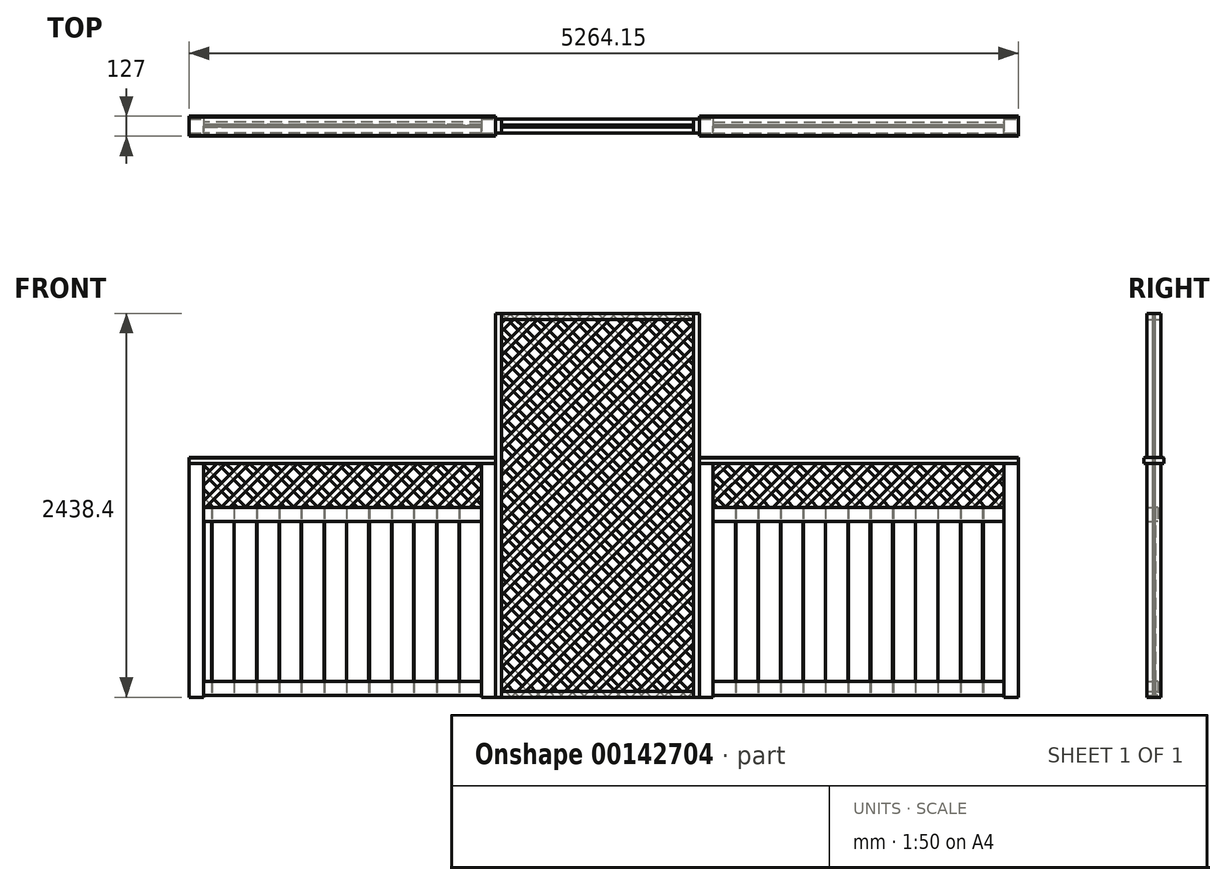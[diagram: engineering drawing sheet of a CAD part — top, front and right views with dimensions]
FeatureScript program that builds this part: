
annotation { "Feature Type Name" : "Feature", "Feature Type Description" : "" }
export const myFeature = defineFeature(function(context is Context, id is Id, definition is map)
    precondition{}
    {
        {
            var Q0;
            Q0=qCreatedBy(makeId("Top.planeOp"),FACE);
            var sketch = newSketch(context, id + "F0", { "sketchPlane" : qUnion([Q0])});
            skLineSegment(sketch, "E0", {"start": v(0, 0) * mm, "end": v(5334, 0) * mm, "construction": true});
            skLineSegment(sketch, "E1.bottom", {"start": v(38.1, 0) * mm, "end": v(127, 0) * mm});
            skLineSegment(sketch, "E1.top", {"start": v(38.1, -88.9) * mm, "end": v(127, -88.9) * mm});
            skLineSegment(sketch, "E1.left", {"start": v(38.1, 0) * mm, "end": v(38.1, -88.9) * mm});
            skLineSegment(sketch, "E1.right", {"start": v(127, 0) * mm, "end": v(127, -88.9) * mm});
            skLineSegment(sketch, "E2.bottom", {"start": v(1892.3, 0) * mm, "end": v(1981.2, 0) * mm});
            skLineSegment(sketch, "E2.top", {"start": v(1892.3, -88.9) * mm, "end": v(1981.2, -88.9) * mm});
            skLineSegment(sketch, "E2.left", {"start": v(1892.3, 0) * mm, "end": v(1892.3, -88.9) * mm});
            skLineSegment(sketch, "E2.right", {"start": v(1981.2, 0) * mm, "end": v(1981.2, -88.9) * mm});
            skLineSegment(sketch, "E3.bottom", {"start": v(3276.6, 0) * mm, "end": v(3365.5, 0) * mm});
            skLineSegment(sketch, "E3.top", {"start": v(3276.6, -88.9) * mm, "end": v(3365.5, -88.9) * mm});
            skLineSegment(sketch, "E3.left", {"start": v(3276.6, 0) * mm, "end": v(3276.6, -88.9) * mm});
            skLineSegment(sketch, "E3.right", {"start": v(3365.5, 0) * mm, "end": v(3365.5, -88.9) * mm});
            skLineSegment(sketch, "E4.bottom", {"start": v(5213.35, 0) * mm, "end": v(5302.25, 0) * mm});
            skLineSegment(sketch, "E4.top", {"start": v(5213.35, -88.9) * mm, "end": v(5302.25, -88.9) * mm});
            skLineSegment(sketch, "E4.left", {"start": v(5213.35, 0) * mm, "end": v(5213.35, -88.9) * mm});
            skLineSegment(sketch, "E4.right", {"start": v(5302.25, 0) * mm, "end": v(5302.25, -88.9) * mm});
            skSolve(sketch);
        }
        {
            var Q0;
            Q0 = qSketchRegion(id + "F0", true);
            extrude(context, id + "F1", {"entities" : qUnion([Q0]), "depth" : 1485.9 * mm});
        }
        {
            var Q0;
            Q0=makeQuery(id+"F1.opExtrude","SWEPT_FACE",FACE,{"disambiguationData":[OSD([sQuery(id+"F0.wireOp",EDGE,"E1.right")])]});
            var sketch = newSketch(context, id + "F2", { "sketchPlane" : qUnion([Q0])});
            skLineSegment(sketch, "E5.bottom", {"start": v(-88.9, 1206.5) * mm, "end": v(-50.8, 1206.5) * mm});
            skLineSegment(sketch, "E5.top", {"start": v(-88.9, 1117.6) * mm, "end": v(-50.8, 1117.6) * mm});
            skLineSegment(sketch, "E5.left", {"start": v(-88.9, 1206.5) * mm, "end": v(-88.9, 1117.6) * mm});
            skLineSegment(sketch, "E5.right", {"start": v(-50.8, 1206.5) * mm, "end": v(-50.8, 1117.6) * mm});
            skSolve(sketch);
        }
        {
            var Q0;
            Q0 = qSketchRegion(id + "F2", true);
            extrude(context, id + "F3", {"entities" : qUnion([Q0]), "depth" : 1765.3 * mm});
        }
        {
            var Q0;
            Q0=makeQuery(id+"F3.opExtrude","SWEPT_BODY",BODY,{"disambiguationData":[OSD([sQuery(id+"F2.wireOp",EDGE,"E5.bottom"),sQuery(id+"F2.wireOp",EDGE,"E5.top"),sQuery(id+"F2.wireOp",EDGE,"E5.left"),sQuery(id+"F2.wireOp",EDGE,"E5.right")])]});
            transform(context, id + "F4", {"entities" : qUnion([Q0]), "transformType" : TransformType.TRANSLATION_3D, "dx" : 0 * mm, "dy" : 0 * mm, "dz" : -1104.9 * mm, "makeCopy" : true});
        }
        {
            var Q0;
            Q0=makeQuery(id+"F1.opExtrude","SWEPT_FACE",FACE,{"disambiguationData":[OSD([sQuery(id+"F0.wireOp",EDGE,"E4.left")])]});
            var sketch = newSketch(context, id + "F5", { "sketchPlane" : qUnion([Q0])});
            skLineSegment(sketch, "E6.bottom", {"start": v(88.9, 1206.5) * mm, "end": v(50.8, 1206.5) * mm});
            skLineSegment(sketch, "E6.top", {"start": v(88.9, 1117.6) * mm, "end": v(50.8, 1117.6) * mm});
            skLineSegment(sketch, "E6.left", {"start": v(88.9, 1206.5) * mm, "end": v(88.9, 1117.6) * mm});
            skLineSegment(sketch, "E6.right", {"start": v(50.8, 1206.5) * mm, "end": v(50.8, 1117.6) * mm});
            skLineSegment(sketch, "E7.bottom", {"start": v(88.9, 101.6) * mm, "end": v(50.8, 101.6) * mm});
            skLineSegment(sketch, "E7.top", {"start": v(88.9, 12.7) * mm, "end": v(50.8, 12.7) * mm});
            skLineSegment(sketch, "E7.left", {"start": v(88.9, 101.6) * mm, "end": v(88.9, 12.7) * mm});
            skLineSegment(sketch, "E7.right", {"start": v(50.8, 101.6) * mm, "end": v(50.8, 12.7) * mm});
            skSolve(sketch);
        }
        {
            var Q0;
            Q0 = qSketchRegion(id + "F5", true);
            extrude(context, id + "F6", {"entities" : qUnion([Q0]), "depth" : 1847.85 * mm});
        }
        {
            var Q0;
            Q0=makeQuery(id+"F1.opExtrude","SWEPT_FACE",FACE,{"disambiguationData":[OSD([sQuery(id+"F0.wireOp",EDGE,"E2.top")])]});
            var sketch = newSketch(context, id + "F7", { "sketchPlane" : qUnion([Q0])});
            skLineSegment(sketch, "E8.bottom", {"start": v(1981.2, 0) * mm, "end": v(2019.3, 0) * mm});
            skLineSegment(sketch, "E8.top", {"start": v(1981.2, 2438.4) * mm, "end": v(2019.3, 2438.4) * mm});
            skLineSegment(sketch, "E8.left", {"start": v(1981.2, 0) * mm, "end": v(1981.2, 2438.4) * mm});
            skLineSegment(sketch, "E8.right", {"start": v(2019.3, 0) * mm, "end": v(2019.3, 2438.4) * mm});
            skSolve(sketch);
        }
        {
            var Q0;
            Q0 = qSketchRegion(id + "F7", true);
            extrude(context, id + "F8", {"entities" : qUnion([Q0]), "oppositeDirection" : true, "depth" : 88.9 * mm});
        }
        {
            var Q0;
            Q0=makeQuery(id+"F1.opExtrude","SWEPT_FACE",FACE,{"disambiguationData":[OSD([sQuery(id+"F0.wireOp",EDGE,"E3.top")])]});
            var sketch = newSketch(context, id + "F9", { "sketchPlane" : qUnion([Q0])});
            skLineSegment(sketch, "E9.bottom", {"start": v(3276.6, 0) * mm, "end": v(3238.5, 0) * mm});
            skLineSegment(sketch, "E9.top", {"start": v(3276.6, 2438.4) * mm, "end": v(3238.5, 2438.4) * mm});
            skLineSegment(sketch, "E9.left", {"start": v(3276.6, 0) * mm, "end": v(3276.6, 2438.4) * mm});
            skLineSegment(sketch, "E9.right", {"start": v(3238.5, 0) * mm, "end": v(3238.5, 2438.4) * mm});
            skSolve(sketch);
        }
        {
            var Q0;
            Q0 = qSketchRegion(id + "F9", true);
            extrude(context, id + "F10", {"entities" : qUnion([Q0]), "oppositeDirection" : true, "depth" : 88.9 * mm});
        }
        {
            var Q0;
            Q0=makeQuery(id+"F8.opExtrude","SWEPT_FACE",FACE,{"disambiguationData":[OSD([sQuery(id+"F7.wireOp",EDGE,"E8.right")])]});
            var sketch = newSketch(context, id + "F11", { "sketchPlane" : qUnion([Q0])});
            skLineSegment(sketch, "E10.bottom", {"start": v(-88.9, 2438.4) * mm, "end": v(-50.8, 2438.4) * mm});
            skLineSegment(sketch, "E10.top", {"start": v(-88.9, 2400.3) * mm, "end": v(-50.8, 2400.3) * mm});
            skLineSegment(sketch, "E10.left", {"start": v(-88.9, 2438.4) * mm, "end": v(-88.9, 2400.3) * mm});
            skLineSegment(sketch, "E10.right", {"start": v(0, 2438.4) * mm, "end": v(0, 2400.3) * mm});
            skLineSegment(sketch, "E11.bottom", {"start": v(-88.9, 0) * mm, "end": v(-50.8, 0) * mm});
            skLineSegment(sketch, "E11.top", {"start": v(-88.9, 38.1) * mm, "end": v(-50.8, 38.1) * mm});
            skLineSegment(sketch, "E11.left", {"start": v(-88.9, 0) * mm, "end": v(-88.9, 38.1) * mm});
            skLineSegment(sketch, "E11.right", {"start": v(0, 0) * mm, "end": v(0, 38.1) * mm});
            skLineSegment(sketch, "E12", {"start": v(-50.8, 2438.4) * mm, "end": v(-50.8, 2400.3) * mm});
            skLineSegment(sketch, "E13", {"start": v(-38.1, 2438.4) * mm, "end": v(-38.1, 2400.3) * mm});
            skLineSegment(sketch, "E14.trimOffspring", {"start": v(-38.1, 2438.4) * mm, "end": v(0, 2438.4) * mm});
            skLineSegment(sketch, "E15.trimOffspring", {"start": v(-38.1, 2400.3) * mm, "end": v(0, 2400.3) * mm});
            skLineSegment(sketch, "E16", {"start": v(-50.8, 38.1) * mm, "end": v(-50.8, 0) * mm});
            skLineSegment(sketch, "E17", {"start": v(-38.1, 38.1) * mm, "end": v(-38.1, 0) * mm});
            skLineSegment(sketch, "E18.trimOffspring", {"start": v(-38.1, 38.1) * mm, "end": v(0, 38.1) * mm});
            skLineSegment(sketch, "E19.trimOffspring", {"start": v(-38.1, 0) * mm, "end": v(0, 0) * mm});
            skSolve(sketch);
        }
        {
            var Q0;
            Q0 = qSketchRegion(id + "F11", true);
            extrude(context, id + "F12", {"entities" : qUnion([Q0]), "depth" : 1219.2 * mm});
        }
        {
            var Q0;
            Q0=makeQuery(id+"F8.opExtrude","CAP_FACE",FACE,{"disambiguationData":[OSD([sQuery(id+"F7.wireOp",EDGE,"E8.bottom"),sQuery(id+"F7.wireOp",EDGE,"E8.top"),sQuery(id+"F7.wireOp",EDGE,"E8.left"),sQuery(id+"F7.wireOp",EDGE,"E8.right")])],"isStart":true});
            cPlane(context, id + "F13", {"entities" : qUnion([Q0]), "cplaneType" : CPlaneType.OFFSET, "offset" : 44.45 * mm, "oppositeDirection" : true, "width" : 152.4 * mm, "height" : 152.4 * mm});
        }
        {
            var Q0;
            Q0=qCreatedBy(id+"F13.planeOp",FACE);
            var sketch = newSketch(context, id + "F14", { "sketchPlane" : qUnion([Q0])});
            skLineSegment(sketch, "E20.bottom", {"start": v(2019.3, 0) * mm, "end": v(3238.5, 0) * mm, "construction": true});
            skLineSegment(sketch, "E20.top", {"start": v(2019.3, 2438.4) * mm, "end": v(3238.5, 2438.4) * mm, "construction": true});
            skLineSegment(sketch, "E20.left", {"start": v(2019.3, 0) * mm, "end": v(2019.3, 2438.4) * mm, "construction": true});
            skLineSegment(sketch, "E20.right", {"start": v(3238.5, 0) * mm, "end": v(3238.5, 2438.4) * mm, "construction": true});
            skLineSegment(sketch, "E21", {"start": v(3201.94, 0) * mm, "end": v(3238.5, 36.56) * mm});
            skLineSegment(sketch, "E22", {"start": v(3238.5, 90.44) * mm, "end": v(3148.06, 0) * mm});
            skLineSegment(sketch, "E23.0.1.0", {"start": v(4481.56, 1485.9) * mm, "end": v(4202.16, 1206.5) * mm});
            skLineSegment(sketch, "E23.0.1.1", {"start": v(3049.54, 0) * mm, "end": v(3238.5, 188.96) * mm});
            skLineSegment(sketch, "E23.0.2.0", {"start": v(4329.16, 1485.9) * mm, "end": v(4049.76, 1206.5) * mm});
            skLineSegment(sketch, "E23.0.2.1", {"start": v(2897.14, 0) * mm, "end": v(3238.5, 341.36) * mm});
            skLineSegment(sketch, "E23.0.3.0", {"start": v(4176.76, 1485.9) * mm, "end": v(3897.36, 1206.5) * mm});
            skLineSegment(sketch, "E23.0.3.1", {"start": v(2744.74, 0) * mm, "end": v(3238.5, 493.76) * mm});
            skLineSegment(sketch, "E23.0.4.0", {"start": v(4024.36, 1485.9) * mm, "end": v(3744.96, 1206.5) * mm});
            skLineSegment(sketch, "E23.0.4.1", {"start": v(2592.34, 0) * mm, "end": v(3238.5, 646.16) * mm});
            skLineSegment(sketch, "E23.0.5.0", {"start": v(3871.96, 1485.9) * mm, "end": v(3592.56, 1206.5) * mm});
            skLineSegment(sketch, "E23.0.5.1", {"start": v(2439.94, 0) * mm, "end": v(3238.5, 798.56) * mm});
            skLineSegment(sketch, "E23.0.6.0", {"start": v(3719.56, 1485.9) * mm, "end": v(3440.16, 1206.5) * mm});
            skLineSegment(sketch, "E23.0.6.1", {"start": v(2287.54, 0) * mm, "end": v(3238.5, 950.96) * mm});
            skLineSegment(sketch, "E23.0.7.0", {"start": v(3567.16, 1485.9) * mm, "end": v(3365.5, 1284.24) * mm});
            skLineSegment(sketch, "E23.0.7.1", {"start": v(2135.14, 0) * mm, "end": v(3238.5, 1103.36) * mm});
            skLineSegment(sketch, "E23.0.8.0", {"start": v(3414.76, 1485.9) * mm, "end": v(3365.5, 1436.64) * mm});
            skLineSegment(sketch, "E23.0.8.1", {"start": v(2019.3, 36.56) * mm, "end": v(3238.5, 1255.76) * mm});
            skLineSegment(sketch, "E23.0.9.0", {"start": v(3238.5, 1462.04) * mm, "end": v(2019.3, 242.84) * mm});
            skLineSegment(sketch, "E23.0.9.1", {"start": v(2019.3, 188.96) * mm, "end": v(3238.5, 1408.16) * mm});
            skLineSegment(sketch, "E23.0.10.0", {"start": v(3238.5, 1614.44) * mm, "end": v(2019.3, 395.24) * mm});
            skLineSegment(sketch, "E23.0.10.1", {"start": v(2019.3, 341.36) * mm, "end": v(3238.5, 1560.56) * mm});
            skLineSegment(sketch, "E23.0.11.0", {"start": v(3238.5, 1766.84) * mm, "end": v(2019.3, 547.64) * mm});
            skLineSegment(sketch, "E23.0.11.1", {"start": v(2019.3, 493.76) * mm, "end": v(3238.5, 1712.96) * mm});
            skLineSegment(sketch, "E23.0.12.0", {"start": v(3238.5, 1919.24) * mm, "end": v(2019.3, 700.04) * mm});
            skLineSegment(sketch, "E23.0.12.1", {"start": v(2019.3, 646.16) * mm, "end": v(3238.5, 1865.36) * mm});
            skLineSegment(sketch, "E23.0.13.0", {"start": v(3238.5, 2071.64) * mm, "end": v(2019.3, 852.44) * mm});
            skLineSegment(sketch, "E23.0.13.1", {"start": v(2019.3, 798.56) * mm, "end": v(3238.5, 2017.76) * mm});
            skLineSegment(sketch, "E23.0.14.0", {"start": v(3238.5, 2224.04) * mm, "end": v(2019.3, 1004.84) * mm});
            skLineSegment(sketch, "E23.0.14.1", {"start": v(2019.3, 950.96) * mm, "end": v(3238.5, 2170.16) * mm});
            skLineSegment(sketch, "E23.0.15.0", {"start": v(3238.5, 2376.44) * mm, "end": v(2019.3, 1157.24) * mm});
            skLineSegment(sketch, "E23.0.15.1", {"start": v(2019.3, 1103.36) * mm, "end": v(3238.5, 2322.56) * mm});
            skLineSegment(sketch, "E23.0.16.0", {"start": v(3148.06, 2438.4) * mm, "end": v(2019.3, 1309.64) * mm});
            skLineSegment(sketch, "E23.0.16.1", {"start": v(2019.3, 1255.76) * mm, "end": v(3201.94, 2438.4) * mm});
            skLineSegment(sketch, "E23.0.17.0", {"start": v(2995.66, 2438.4) * mm, "end": v(2019.3, 1462.04) * mm});
            skLineSegment(sketch, "E23.0.17.1", {"start": v(1817.64, 1206.5) * mm, "end": v(1892.3, 1281.16) * mm});
            skLineSegment(sketch, "E23.0.18.0", {"start": v(2843.26, 2438.4) * mm, "end": v(2019.3, 1614.44) * mm});
            skLineSegment(sketch, "E23.0.18.1", {"start": v(1665.24, 1206.5) * mm, "end": v(1892.3, 1433.56) * mm});
            skLineSegment(sketch, "E23.0.19.0", {"start": v(2690.86, 2438.4) * mm, "end": v(2019.3, 1766.84) * mm});
            skLineSegment(sketch, "E23.0.19.1", {"start": v(1512.84, 1206.5) * mm, "end": v(1792.24, 1485.9) * mm});
            skLineSegment(sketch, "E23.0.20.0", {"start": v(2538.46, 2438.4) * mm, "end": v(2019.3, 1919.24) * mm});
            skLineSegment(sketch, "E23.0.20.1", {"start": v(2019.3, 1865.36) * mm, "end": v(2592.34, 2438.4) * mm});
            skLineSegment(sketch, "E23.0.21.0", {"start": v(2386.06, 2438.4) * mm, "end": v(2019.3, 2071.64) * mm});
            skLineSegment(sketch, "E23.0.21.1", {"start": v(2019.3, 2017.76) * mm, "end": v(2439.94, 2438.4) * mm});
            skLineSegment(sketch, "E23.0.22.0", {"start": v(2233.66, 2438.4) * mm, "end": v(2019.3, 2224.04) * mm});
            skLineSegment(sketch, "E23.0.22.1", {"start": v(2019.3, 2170.16) * mm, "end": v(2287.54, 2438.4) * mm});
            skLineSegment(sketch, "E23.0.23.0", {"start": v(2081.26, 2438.4) * mm, "end": v(2019.3, 2376.44) * mm});
            skLineSegment(sketch, "E23.0.23.1", {"start": v(2019.3, 2322.56) * mm, "end": v(2135.14, 2438.4) * mm});
            skLineSegment(sketch, "E23.direction2", {"start": v(3238.5, 90.44) * mm, "end": v(3238.5, 242.84) * mm, "construction": true});
            skPoint(sketch, "E24.start.orphan", {"position": v(3265.44, 63.5) * mm});
            skLineSegment(sketch, "E25", {"start": v(2081.26, 2438.4) * mm, "end": v(2135.14, 2438.4) * mm});
            skLineSegment(sketch, "E26", {"start": v(2233.66, 2438.4) * mm, "end": v(2287.54, 2438.4) * mm});
            skLineSegment(sketch, "E27", {"start": v(2386.06, 2438.4) * mm, "end": v(2439.94, 2438.4) * mm});
            skLineSegment(sketch, "E28", {"start": v(2538.46, 2438.4) * mm, "end": v(2592.34, 2438.4) * mm});
            skLineSegment(sketch, "E29", {"start": v(2690.86, 2438.4) * mm, "end": v(2744.74, 2438.4) * mm});
            skLineSegment(sketch, "E30", {"start": v(2843.26, 2438.4) * mm, "end": v(2897.14, 2438.4) * mm});
            skLineSegment(sketch, "E31", {"start": v(2995.66, 2438.4) * mm, "end": v(3049.54, 2438.4) * mm});
            skLineSegment(sketch, "E32", {"start": v(3148.06, 2438.4) * mm, "end": v(3201.94, 2438.4) * mm});
            skLineSegment(sketch, "E33", {"start": v(3238.5, 2376.44) * mm, "end": v(3238.5, 2322.56) * mm});
            skLineSegment(sketch, "E34", {"start": v(3238.5, 2224.04) * mm, "end": v(3238.5, 2170.16) * mm});
            skLineSegment(sketch, "E35", {"start": v(3238.5, 2071.64) * mm, "end": v(3238.5, 2017.76) * mm});
            skLineSegment(sketch, "E36", {"start": v(3238.5, 1919.24) * mm, "end": v(3238.5, 1865.36) * mm});
            skLineSegment(sketch, "E37", {"start": v(3238.5, 1766.84) * mm, "end": v(3238.5, 1712.96) * mm});
            skLineSegment(sketch, "E38", {"start": v(3238.5, 1614.44) * mm, "end": v(3238.5, 1560.56) * mm});
            skLineSegment(sketch, "E39", {"start": v(3238.5, 1462.04) * mm, "end": v(3238.5, 1408.16) * mm});
            skLineSegment(sketch, "E40", {"start": v(3238.5, 1309.64) * mm, "end": v(3238.5, 1255.76) * mm});
            skLineSegment(sketch, "E41", {"start": v(3238.5, 1157.24) * mm, "end": v(3238.5, 1103.36) * mm});
            skLineSegment(sketch, "E42", {"start": v(3238.5, 1004.84) * mm, "end": v(3238.5, 950.96) * mm});
            skLineSegment(sketch, "E43", {"start": v(3238.5, 852.44) * mm, "end": v(3238.5, 798.56) * mm});
            skLineSegment(sketch, "E44", {"start": v(3238.5, 700.04) * mm, "end": v(3238.5, 646.16) * mm});
            skLineSegment(sketch, "E45", {"start": v(3238.5, 547.64) * mm, "end": v(3238.5, 493.76) * mm});
            skLineSegment(sketch, "E46", {"start": v(3238.5, 395.24) * mm, "end": v(3238.5, 341.36) * mm});
            skLineSegment(sketch, "E47", {"start": v(3238.5, 242.84) * mm, "end": v(3238.5, 188.96) * mm});
            skLineSegment(sketch, "E48", {"start": v(3238.5, 36.56) * mm, "end": v(3238.5, 90.44) * mm});
            skLineSegment(sketch, "E49", {"start": v(3201.94, 0) * mm, "end": v(3148.06, 0) * mm});
            skLineSegment(sketch, "E50", {"start": v(3049.54, 0) * mm, "end": v(2995.66, 0) * mm});
            skLineSegment(sketch, "E51", {"start": v(2897.14, 0) * mm, "end": v(2843.26, 0) * mm});
            skLineSegment(sketch, "E52", {"start": v(2744.74, 0) * mm, "end": v(2690.86, 0) * mm});
            skLineSegment(sketch, "E53", {"start": v(2592.34, 0) * mm, "end": v(2538.46, 0) * mm});
            skLineSegment(sketch, "E54", {"start": v(2439.94, 0) * mm, "end": v(2386.06, 0) * mm});
            skLineSegment(sketch, "E55", {"start": v(2287.54, 0) * mm, "end": v(2233.66, 0) * mm});
            skLineSegment(sketch, "E56", {"start": v(2135.14, 0) * mm, "end": v(2081.26, 0) * mm});
            skLineSegment(sketch, "E57", {"start": v(2019.3, 36.56) * mm, "end": v(2019.3, 90.44) * mm});
            skLineSegment(sketch, "E58", {"start": v(2019.3, 188.96) * mm, "end": v(2019.3, 242.84) * mm});
            skLineSegment(sketch, "E59", {"start": v(2019.3, 341.36) * mm, "end": v(2019.3, 395.24) * mm});
            skLineSegment(sketch, "E60", {"start": v(2019.3, 493.76) * mm, "end": v(2019.3, 547.64) * mm});
            skLineSegment(sketch, "E61", {"start": v(2019.3, 646.16) * mm, "end": v(2019.3, 700.04) * mm});
            skLineSegment(sketch, "E62", {"start": v(2019.3, 798.56) * mm, "end": v(2019.3, 852.44) * mm});
            skLineSegment(sketch, "E63", {"start": v(2019.3, 950.96) * mm, "end": v(2019.3, 1004.84) * mm});
            skLineSegment(sketch, "E64", {"start": v(2019.3, 1103.36) * mm, "end": v(2019.3, 1157.24) * mm});
            skLineSegment(sketch, "E65", {"start": v(2019.3, 1255.76) * mm, "end": v(2019.3, 1309.64) * mm});
            skLineSegment(sketch, "E66", {"start": v(2019.3, 1408.16) * mm, "end": v(2019.3, 1462.04) * mm});
            skLineSegment(sketch, "E67", {"start": v(2019.3, 1560.56) * mm, "end": v(2019.3, 1614.44) * mm});
            skLineSegment(sketch, "E68", {"start": v(2019.3, 1712.96) * mm, "end": v(2019.3, 1766.84) * mm});
            skLineSegment(sketch, "E69", {"start": v(2019.3, 1865.36) * mm, "end": v(2019.3, 1919.24) * mm});
            skLineSegment(sketch, "E70", {"start": v(2019.3, 2017.76) * mm, "end": v(2019.3, 2071.64) * mm});
            skLineSegment(sketch, "E71", {"start": v(2019.3, 2170.16) * mm, "end": v(2019.3, 2224.04) * mm});
            skLineSegment(sketch, "E72", {"start": v(2019.3, 2322.56) * mm, "end": v(2019.3, 2376.44) * mm});
            skLineSegment(sketch, "E73.bottom", {"start": v(1892.3, 1485.9) * mm, "end": v(127, 1485.9) * mm, "construction": true});
            skLineSegment(sketch, "E73.top", {"start": v(1892.3, 1206.5) * mm, "end": v(127, 1206.5) * mm, "construction": true});
            skLineSegment(sketch, "E73.left", {"start": v(1892.3, 1485.9) * mm, "end": v(1892.3, 1206.5) * mm, "construction": true});
            skLineSegment(sketch, "E73.right", {"start": v(127, 1485.9) * mm, "end": v(127, 1206.5) * mm, "construction": true});
            skLineSegment(sketch, "E74.trimOffspring", {"start": v(1890.76, 1485.9) * mm, "end": v(1611.36, 1206.5) * mm});
            skLineSegment(sketch, "E75.trimOffspring", {"start": v(2019.3, 1560.56) * mm, "end": v(2897.14, 2438.4) * mm});
            skLineSegment(sketch, "E76.trimOffspring", {"start": v(1892.3, 1335.04) * mm, "end": v(1763.76, 1206.5) * mm});
            skLineSegment(sketch, "E77.trimOffspring", {"start": v(2019.3, 1408.16) * mm, "end": v(3049.54, 2438.4) * mm});
            skLineSegment(sketch, "E78", {"start": v(1892.3, 1433.56) * mm, "end": v(1892.3, 1485.9) * mm});
            skLineSegment(sketch, "E79", {"start": v(1892.3, 1281.16) * mm, "end": v(1892.3, 1335.04) * mm});
            skLineSegment(sketch, "E80", {"start": v(1817.64, 1206.5) * mm, "end": v(1763.76, 1206.5) * mm});
            skLineSegment(sketch, "E81", {"start": v(1665.24, 1206.5) * mm, "end": v(1611.36, 1206.5) * mm});
            skLineSegment(sketch, "E82", {"start": v(1611.36, 1206.5) * mm, "end": v(1665.24, 1206.5) * mm});
            skLineSegment(sketch, "E83", {"start": v(1890.76, 1485.9) * mm, "end": v(1892.3, 1485.9) * mm});
            skLineSegment(sketch, "E84.trimOffspring", {"start": v(1738.36, 1485.9) * mm, "end": v(1458.96, 1206.5) * mm});
            skLineSegment(sketch, "E85.trimOffspring", {"start": v(2019.3, 1712.96) * mm, "end": v(2744.74, 2438.4) * mm});
            skLineSegment(sketch, "E86", {"start": v(1792.24, 1485.9) * mm, "end": v(1738.36, 1485.9) * mm});
            skLineSegment(sketch, "E87", {"start": v(1512.84, 1206.5) * mm, "end": v(1458.96, 1206.5) * mm});
            skLineSegment(sketch, "E88.1.0.0", {"start": v(1360.44, 1206.5) * mm, "end": v(1639.84, 1485.9) * mm});
            skLineSegment(sketch, "E88.1.0.1", {"start": v(1585.96, 1485.9) * mm, "end": v(1306.56, 1206.5) * mm});
            skLineSegment(sketch, "E88.2.0.0", {"start": v(1208.04, 1206.5) * mm, "end": v(1487.44, 1485.9) * mm});
            skLineSegment(sketch, "E88.2.0.1", {"start": v(1433.56, 1485.9) * mm, "end": v(1154.16, 1206.5) * mm});
            skLineSegment(sketch, "E88.3.0.0", {"start": v(1055.64, 1206.5) * mm, "end": v(1335.04, 1485.9) * mm});
            skLineSegment(sketch, "E88.3.0.1", {"start": v(1281.16, 1485.9) * mm, "end": v(1001.76, 1206.5) * mm});
            skLineSegment(sketch, "E88.4.0.0", {"start": v(903.24, 1206.5) * mm, "end": v(1182.64, 1485.9) * mm});
            skLineSegment(sketch, "E88.4.0.1", {"start": v(1128.76, 1485.9) * mm, "end": v(849.36, 1206.5) * mm});
            skLineSegment(sketch, "E88.5.0.0", {"start": v(750.84, 1206.5) * mm, "end": v(1030.24, 1485.9) * mm});
            skLineSegment(sketch, "E88.5.0.1", {"start": v(976.36, 1485.9) * mm, "end": v(696.96, 1206.5) * mm});
            skLineSegment(sketch, "E88.6.0.0", {"start": v(598.44, 1206.5) * mm, "end": v(877.84, 1485.9) * mm});
            skLineSegment(sketch, "E88.6.0.1", {"start": v(823.96, 1485.9) * mm, "end": v(544.56, 1206.5) * mm});
            skLineSegment(sketch, "E88.7.0.0", {"start": v(446.04, 1206.5) * mm, "end": v(725.44, 1485.9) * mm});
            skLineSegment(sketch, "E88.7.0.1", {"start": v(671.56, 1485.9) * mm, "end": v(392.16, 1206.5) * mm});
            skLineSegment(sketch, "E88.8.0.0", {"start": v(293.64, 1206.5) * mm, "end": v(573.04, 1485.9) * mm});
            skLineSegment(sketch, "E88.8.0.1", {"start": v(519.16, 1485.9) * mm, "end": v(239.76, 1206.5) * mm});
            skLineSegment(sketch, "E88.9.0.0", {"start": v(141.24, 1206.5) * mm, "end": v(420.64, 1485.9) * mm});
            skLineSegment(sketch, "E88.9.0.1", {"start": v(366.76, 1485.9) * mm, "end": v(127, 1246.14) * mm});
            skLineSegment(sketch, "E88.10.0.0", {"start": v(127, 1344.66) * mm, "end": v(268.24, 1485.9) * mm});
            skLineSegment(sketch, "E88.10.0.1", {"start": v(214.36, 1485.9) * mm, "end": v(127, 1398.54) * mm});
            skLineSegment(sketch, "E88.direction1", {"start": v(1512.84, 1206.5) * mm, "end": v(1360.44, 1206.5) * mm, "construction": true});
            skLineSegment(sketch, "E89", {"start": v(1360.44, 1206.5) * mm, "end": v(1306.56, 1206.5) * mm});
            skLineSegment(sketch, "E90", {"start": v(1208.04, 1206.5) * mm, "end": v(1154.16, 1206.5) * mm});
            skLineSegment(sketch, "E91", {"start": v(1639.84, 1485.9) * mm, "end": v(1585.96, 1485.9) * mm});
            skLineSegment(sketch, "E92", {"start": v(1487.44, 1485.9) * mm, "end": v(1433.56, 1485.9) * mm});
            skLineSegment(sketch, "E93", {"start": v(1335.04, 1485.9) * mm, "end": v(1281.16, 1485.9) * mm});
            skLineSegment(sketch, "E94", {"start": v(1182.64, 1485.9) * mm, "end": v(1128.76, 1485.9) * mm});
            skLineSegment(sketch, "E95", {"start": v(1030.24, 1485.9) * mm, "end": v(976.36, 1485.9) * mm});
            skLineSegment(sketch, "E96", {"start": v(1055.64, 1206.5) * mm, "end": v(1001.76, 1206.5) * mm});
            skLineSegment(sketch, "E97", {"start": v(544.56, 1206.5) * mm, "end": v(598.44, 1206.5) * mm});
            skLineSegment(sketch, "E98", {"start": v(696.96, 1206.5) * mm, "end": v(750.84, 1206.5) * mm});
            skLineSegment(sketch, "E99", {"start": v(849.36, 1206.5) * mm, "end": v(903.24, 1206.5) * mm});
            skLineSegment(sketch, "E100", {"start": v(366.76, 1485.9) * mm, "end": v(420.64, 1485.9) * mm});
            skLineSegment(sketch, "E101", {"start": v(519.16, 1485.9) * mm, "end": v(573.04, 1485.9) * mm});
            skLineSegment(sketch, "E102", {"start": v(671.56, 1485.9) * mm, "end": v(725.44, 1485.9) * mm});
            skLineSegment(sketch, "E103", {"start": v(823.96, 1485.9) * mm, "end": v(877.84, 1485.9) * mm});
            skLineSegment(sketch, "E104", {"start": v(446.04, 1206.5) * mm, "end": v(392.16, 1206.5) * mm});
            skLineSegment(sketch, "E105", {"start": v(293.64, 1206.5) * mm, "end": v(239.76, 1206.5) * mm});
            skLineSegment(sketch, "E106", {"start": v(141.24, 1206.5) * mm, "end": v(127, 1206.5) * mm});
            skLineSegment(sketch, "E107", {"start": v(127, 1398.54) * mm, "end": v(127, 1344.66) * mm});
            skLineSegment(sketch, "E108", {"start": v(268.24, 1485.9) * mm, "end": v(214.36, 1485.9) * mm});
            skLineSegment(sketch, "E109", {"start": v(127, 1246.14) * mm, "end": v(127, 1206.5) * mm});
            skLineSegment(sketch, "E110.bottom", {"start": v(3365.5, 1485.9) * mm, "end": v(5213.35, 1485.9) * mm, "construction": true});
            skLineSegment(sketch, "E110.top", {"start": v(3365.5, 1206.5) * mm, "end": v(5213.35, 1206.5) * mm, "construction": true});
            skLineSegment(sketch, "E110.left", {"start": v(3365.5, 1485.9) * mm, "end": v(3365.5, 1206.5) * mm, "construction": true});
            skLineSegment(sketch, "E110.right", {"start": v(5213.35, 1485.9) * mm, "end": v(5213.35, 1206.5) * mm, "construction": true});
            skLineSegment(sketch, "E111.trimOffspring", {"start": v(4256.04, 1206.5) * mm, "end": v(4535.44, 1485.9) * mm});
            skLineSegment(sketch, "E112.trimOffspring", {"start": v(3238.5, 242.84) * mm, "end": v(2995.66, 0) * mm});
            skLineSegment(sketch, "E113.trimOffspring", {"start": v(4103.64, 1206.5) * mm, "end": v(4383.04, 1485.9) * mm});
            skLineSegment(sketch, "E114.trimOffspring", {"start": v(3238.5, 395.24) * mm, "end": v(2843.26, 0) * mm});
            skLineSegment(sketch, "E115.trimOffspring", {"start": v(3951.24, 1206.5) * mm, "end": v(4230.64, 1485.9) * mm});
            skLineSegment(sketch, "E116.trimOffspring", {"start": v(3238.5, 547.64) * mm, "end": v(2690.86, 0) * mm});
            skLineSegment(sketch, "E117.trimOffspring", {"start": v(3238.5, 700.04) * mm, "end": v(2538.46, 0) * mm});
            skLineSegment(sketch, "E118.trimOffspring", {"start": v(3494.04, 1206.5) * mm, "end": v(3773.44, 1485.9) * mm});
            skLineSegment(sketch, "E119.trimOffspring", {"start": v(3238.5, 1004.84) * mm, "end": v(2233.66, 0) * mm});
            skLineSegment(sketch, "E120.trimOffspring", {"start": v(3798.84, 1206.5) * mm, "end": v(4078.24, 1485.9) * mm});
            skLineSegment(sketch, "E121.trimOffspring", {"start": v(3646.44, 1206.5) * mm, "end": v(3925.84, 1485.9) * mm});
            skLineSegment(sketch, "E122.trimOffspring", {"start": v(3238.5, 852.44) * mm, "end": v(2386.06, 0) * mm});
            skLineSegment(sketch, "E123.trimOffspring", {"start": v(3238.5, 1309.64) * mm, "end": v(2019.3, 90.44) * mm});
            skLineSegment(sketch, "E124.trimOffspring", {"start": v(3365.5, 1382.76) * mm, "end": v(3468.64, 1485.9) * mm});
            skLineSegment(sketch, "E125.trimOffspring", {"start": v(3238.5, 1157.24) * mm, "end": v(2081.26, 0) * mm});
            skLineSegment(sketch, "E126.trimOffspring", {"start": v(3365.5, 1230.36) * mm, "end": v(3621.04, 1485.9) * mm});
            skLineSegment(sketch, "E127.1.0.0", {"start": v(4633.96, 1485.9) * mm, "end": v(4354.56, 1206.5) * mm});
            skLineSegment(sketch, "E127.1.0.1", {"start": v(4408.44, 1206.5) * mm, "end": v(4687.84, 1485.9) * mm});
            skLineSegment(sketch, "E127.2.0.0", {"start": v(4786.36, 1485.9) * mm, "end": v(4506.96, 1206.5) * mm});
            skLineSegment(sketch, "E127.2.0.1", {"start": v(4560.84, 1206.5) * mm, "end": v(4840.24, 1485.9) * mm});
            skLineSegment(sketch, "E127.3.0.0", {"start": v(4938.76, 1485.9) * mm, "end": v(4659.36, 1206.5) * mm});
            skLineSegment(sketch, "E127.3.0.1", {"start": v(4713.24, 1206.5) * mm, "end": v(4992.64, 1485.9) * mm});
            skLineSegment(sketch, "E127.4.0.0", {"start": v(5091.16, 1485.9) * mm, "end": v(4811.76, 1206.5) * mm});
            skLineSegment(sketch, "E127.4.0.1", {"start": v(4865.64, 1206.5) * mm, "end": v(5145.04, 1485.9) * mm});
            skLineSegment(sketch, "E127.5.0.0", {"start": v(5213.35, 1455.7) * mm, "end": v(4964.16, 1206.5) * mm});
            skLineSegment(sketch, "E127.5.0.1", {"start": v(5018.04, 1206.5) * mm, "end": v(5213.35, 1401.8) * mm});
            skLineSegment(sketch, "E127.6.0.0", {"start": v(5213.35, 1303.3) * mm, "end": v(5116.56, 1206.5) * mm});
            skLineSegment(sketch, "E127.6.0.1", {"start": v(5170.44, 1206.5) * mm, "end": v(5213.35, 1249.4) * mm});
            skLineSegment(sketch, "E127.direction1", {"start": v(4202.16, 1206.5) * mm, "end": v(4354.56, 1206.5) * mm, "construction": true});
            skLineSegment(sketch, "E128", {"start": v(5213.35, 1455.7) * mm, "end": v(5213.35, 1401.8) * mm});
            skLineSegment(sketch, "E129", {"start": v(5213.35, 1303.3) * mm, "end": v(5213.35, 1249.4) * mm});
            skLineSegment(sketch, "E130", {"start": v(5170.44, 1206.5) * mm, "end": v(5116.56, 1206.5) * mm});
            skLineSegment(sketch, "E131", {"start": v(5018.04, 1206.5) * mm, "end": v(4964.16, 1206.5) * mm});
            skLineSegment(sketch, "E132", {"start": v(4865.64, 1206.5) * mm, "end": v(4811.76, 1206.5) * mm});
            skLineSegment(sketch, "E133", {"start": v(4713.24, 1206.5) * mm, "end": v(4659.36, 1206.5) * mm});
            skLineSegment(sketch, "E134", {"start": v(4560.84, 1206.5) * mm, "end": v(4506.96, 1206.5) * mm});
            skLineSegment(sketch, "E135", {"start": v(4633.96, 1485.9) * mm, "end": v(4687.84, 1485.9) * mm});
            skLineSegment(sketch, "E136", {"start": v(4786.36, 1485.9) * mm, "end": v(4840.24, 1485.9) * mm});
            skLineSegment(sketch, "E137", {"start": v(4938.76, 1485.9) * mm, "end": v(4992.64, 1485.9) * mm});
            skLineSegment(sketch, "E138", {"start": v(5091.16, 1485.9) * mm, "end": v(5145.04, 1485.9) * mm});
            skLineSegment(sketch, "E139", {"start": v(3365.5, 1436.64) * mm, "end": v(3365.5, 1382.76) * mm});
            skLineSegment(sketch, "E140", {"start": v(3365.5, 1230.36) * mm, "end": v(3365.5, 1284.24) * mm});
            skLineSegment(sketch, "E141", {"start": v(3440.16, 1206.5) * mm, "end": v(3494.04, 1206.5) * mm});
            skLineSegment(sketch, "E142", {"start": v(3592.56, 1206.5) * mm, "end": v(3646.44, 1206.5) * mm});
            skLineSegment(sketch, "E143", {"start": v(3744.96, 1206.5) * mm, "end": v(3798.84, 1206.5) * mm});
            skLineSegment(sketch, "E144", {"start": v(3897.36, 1206.5) * mm, "end": v(3951.24, 1206.5) * mm});
            skLineSegment(sketch, "E145", {"start": v(4049.76, 1206.5) * mm, "end": v(4103.64, 1206.5) * mm});
            skLineSegment(sketch, "E146", {"start": v(4202.16, 1206.5) * mm, "end": v(4256.04, 1206.5) * mm});
            skLineSegment(sketch, "E147", {"start": v(3414.76, 1485.9) * mm, "end": v(3468.64, 1485.9) * mm});
            skLineSegment(sketch, "E148", {"start": v(3567.16, 1485.9) * mm, "end": v(3621.04, 1485.9) * mm});
            skLineSegment(sketch, "E149", {"start": v(3719.56, 1485.9) * mm, "end": v(3773.44, 1485.9) * mm});
            skLineSegment(sketch, "E150", {"start": v(3871.96, 1485.9) * mm, "end": v(3925.84, 1485.9) * mm});
            skLineSegment(sketch, "E151", {"start": v(4024.36, 1485.9) * mm, "end": v(4078.24, 1485.9) * mm});
            skLineSegment(sketch, "E152", {"start": v(4176.76, 1485.9) * mm, "end": v(4230.64, 1485.9) * mm});
            skLineSegment(sketch, "E153", {"start": v(4329.16, 1485.9) * mm, "end": v(4383.04, 1485.9) * mm});
            skLineSegment(sketch, "E154", {"start": v(4481.56, 1485.9) * mm, "end": v(4535.44, 1485.9) * mm});
            skLineSegment(sketch, "E155", {"start": v(4408.44, 1206.5) * mm, "end": v(4354.56, 1206.5) * mm});
            skSolve(sketch);
        }
        {
            var Q0;
            Q0 = qSketchRegion(id + "F14", true);
            var Q1;
            Q1=makeQuery(id+"F14.imprint","IMPRINT",FACE,{"disambiguationData":[TD([[makeQuery(id+"F14.imprint","IMPRINT",EDGE,{"derivedFrom":sQuery(id+"F14.wireOp",EDGE,"E23.0.16.0")}),1.0]])]});
            extrude(context, id + "F15", {"entities" : qUnion([Q0, Q1]), "depth" : 6.35 * mm});
        }
        {
            var Q0;
            Q0=qCreatedBy(id+"F13.planeOp",FACE);
            var sketch = newSketch(context, id + "F16", { "sketchPlane" : qUnion([Q0])});
            skLineSegment(sketch, "E156.bottom", {"start": v(2019.3, 0) * mm, "end": v(3238.5, 0) * mm, "construction": true});
            skLineSegment(sketch, "E156.top", {"start": v(2019.3, 2438.4) * mm, "end": v(3238.5, 2438.4) * mm, "construction": true});
            skLineSegment(sketch, "E156.right", {"start": v(3238.5, 0) * mm, "end": v(3238.5, 2438.4) * mm, "construction": true});
            skLineSegment(sketch, "E157", {"start": v(2019.3, 63.5) * mm, "end": v(2082.8, 0) * mm});
            skLineSegment(sketch, "E158", {"start": v(2136.68, 0) * mm, "end": v(2019.3, 117.38) * mm});
            skLineSegment(sketch, "E159", {"start": v(2019.3, 117.38) * mm, "end": v(2019.3, 63.5) * mm});
            skLineSegment(sketch, "E160.0.1.0", {"start": v(2019.3, 257.08) * mm, "end": v(2019.3, 203.2) * mm});
            skLineSegment(sketch, "E160.0.1.1", {"start": v(2276.38, 0) * mm, "end": v(2019.3, 257.08) * mm});
            skLineSegment(sketch, "E160.0.1.2", {"start": v(2019.3, 203.2) * mm, "end": v(2222.5, 0) * mm});
            skLineSegment(sketch, "E160.0.2.0", {"start": v(2019.3, 396.78) * mm, "end": v(2019.3, 342.9) * mm});
            skLineSegment(sketch, "E160.0.2.1", {"start": v(2416.08, 0) * mm, "end": v(2019.3, 396.78) * mm});
            skLineSegment(sketch, "E160.0.2.2", {"start": v(2019.3, 342.9) * mm, "end": v(2362.2, 0) * mm});
            skLineSegment(sketch, "E160.0.3.0", {"start": v(2019.3, 536.48) * mm, "end": v(2019.3, 482.6) * mm});
            skLineSegment(sketch, "E160.0.3.1", {"start": v(2555.78, 0) * mm, "end": v(2019.3, 536.48) * mm});
            skLineSegment(sketch, "E160.0.3.2", {"start": v(2019.3, 482.6) * mm, "end": v(2501.9, 0) * mm});
            skLineSegment(sketch, "E160.0.4.0", {"start": v(2019.3, 676.18) * mm, "end": v(2019.3, 622.3) * mm});
            skLineSegment(sketch, "E160.0.4.1", {"start": v(2695.48, 0) * mm, "end": v(2019.3, 676.18) * mm});
            skLineSegment(sketch, "E160.0.4.2", {"start": v(2019.3, 622.3) * mm, "end": v(2641.6, 0) * mm});
            skLineSegment(sketch, "E160.0.5.0", {"start": v(2019.3, 815.88) * mm, "end": v(2019.3, 762) * mm});
            skLineSegment(sketch, "E160.0.5.1", {"start": v(2835.18, 0) * mm, "end": v(2019.3, 815.88) * mm});
            skLineSegment(sketch, "E160.0.5.2", {"start": v(2019.3, 762) * mm, "end": v(2781.3, 0) * mm});
            skLineSegment(sketch, "E160.0.6.0", {"start": v(2019.3, 955.58) * mm, "end": v(2019.3, 901.7) * mm});
            skLineSegment(sketch, "E160.0.6.1", {"start": v(2974.88, 0) * mm, "end": v(2019.3, 955.58) * mm});
            skLineSegment(sketch, "E160.0.6.2", {"start": v(1435.1, 1485.9) * mm, "end": v(1714.5, 1206.5) * mm});
            skLineSegment(sketch, "E160.0.7.0", {"start": v(2019.3, 1095.28) * mm, "end": v(2019.3, 1041.4) * mm});
            skLineSegment(sketch, "E160.0.7.1", {"start": v(3114.58, 0) * mm, "end": v(2019.3, 1095.28) * mm});
            skLineSegment(sketch, "E160.0.7.2", {"start": v(1574.8, 1485.9) * mm, "end": v(1854.2, 1206.5) * mm});
            skLineSegment(sketch, "E160.0.8.0", {"start": v(2019.3, 1234.98) * mm, "end": v(2019.3, 1181.1) * mm});
            skLineSegment(sketch, "E160.0.8.1", {"start": v(3238.5, 15.78) * mm, "end": v(2019.3, 1234.98) * mm});
            skLineSegment(sketch, "E160.0.8.2", {"start": v(1714.5, 1485.9) * mm, "end": v(1892.3, 1308.1) * mm});
            skLineSegment(sketch, "E160.0.9.0", {"start": v(2019.3, 1374.68) * mm, "end": v(2019.3, 1320.8) * mm});
            skLineSegment(sketch, "E160.0.9.1", {"start": v(3238.5, 155.48) * mm, "end": v(2019.3, 1374.68) * mm});
            skLineSegment(sketch, "E160.0.9.2", {"start": v(1854.2, 1485.9) * mm, "end": v(1892.3, 1447.8) * mm});
            skLineSegment(sketch, "E160.0.10.0", {"start": v(2019.3, 1514.38) * mm, "end": v(2019.3, 1460.5) * mm});
            skLineSegment(sketch, "E160.0.10.1", {"start": v(3238.5, 295.18) * mm, "end": v(2019.3, 1514.38) * mm});
            skLineSegment(sketch, "E160.0.10.2", {"start": v(2019.3, 1460.5) * mm, "end": v(3238.5, 241.3) * mm});
            skLineSegment(sketch, "E160.0.11.0", {"start": v(2019.3, 1654.08) * mm, "end": v(2019.3, 1600.2) * mm});
            skLineSegment(sketch, "E160.0.11.1", {"start": v(3238.5, 434.88) * mm, "end": v(2019.3, 1654.08) * mm});
            skLineSegment(sketch, "E160.0.11.2", {"start": v(2019.3, 1600.2) * mm, "end": v(3238.5, 381) * mm});
            skLineSegment(sketch, "E160.0.12.0", {"start": v(2019.3, 1793.78) * mm, "end": v(2019.3, 1739.9) * mm});
            skLineSegment(sketch, "E160.0.12.1", {"start": v(3238.5, 574.58) * mm, "end": v(2019.3, 1793.78) * mm});
            skLineSegment(sketch, "E160.0.12.2", {"start": v(2019.3, 1739.9) * mm, "end": v(3238.5, 520.7) * mm});
            skLineSegment(sketch, "E160.0.13.0", {"start": v(2019.3, 1933.48) * mm, "end": v(2019.3, 1879.6) * mm});
            skLineSegment(sketch, "E160.0.13.1", {"start": v(3238.5, 714.28) * mm, "end": v(2019.3, 1933.48) * mm});
            skLineSegment(sketch, "E160.0.13.2", {"start": v(2019.3, 1879.6) * mm, "end": v(3238.5, 660.4) * mm});
            skLineSegment(sketch, "E160.0.14.0", {"start": v(2019.3, 2073.18) * mm, "end": v(2019.3, 2019.3) * mm});
            skLineSegment(sketch, "E160.0.14.1", {"start": v(3238.5, 853.98) * mm, "end": v(2019.3, 2073.18) * mm});
            skLineSegment(sketch, "E160.0.14.2", {"start": v(2019.3, 2019.3) * mm, "end": v(3238.5, 800.1) * mm});
            skLineSegment(sketch, "E160.0.15.0", {"start": v(2019.3, 2212.88) * mm, "end": v(2019.3, 2159) * mm});
            skLineSegment(sketch, "E160.0.15.1", {"start": v(3238.5, 993.68) * mm, "end": v(2019.3, 2212.88) * mm});
            skLineSegment(sketch, "E160.0.15.2", {"start": v(2019.3, 2159) * mm, "end": v(3238.5, 939.8) * mm});
            skLineSegment(sketch, "E160.0.16.0", {"start": v(2019.3, 2352.58) * mm, "end": v(2019.3, 2298.7) * mm});
            skLineSegment(sketch, "E160.0.16.1", {"start": v(3238.5, 1133.38) * mm, "end": v(2019.3, 2352.58) * mm});
            skLineSegment(sketch, "E160.0.16.2", {"start": v(2019.3, 2298.7) * mm, "end": v(3238.5, 1079.5) * mm});
            skLineSegment(sketch, "E160.0.17.1", {"start": v(3238.5, 1273.08) * mm, "end": v(2073.18, 2438.4) * mm});
            skLineSegment(sketch, "E160.0.17.2", {"start": v(2019.3, 2438.4) * mm, "end": v(3238.5, 1219.2) * mm});
            skLineSegment(sketch, "E160.0.18.2", {"start": v(2159, 2438.4) * mm, "end": v(3238.5, 1358.9) * mm});
            skLineSegment(sketch, "E160.0.19.2", {"start": v(2298.7, 2438.4) * mm, "end": v(3238.5, 1498.6) * mm});
            skLineSegment(sketch, "E160.0.20.2", {"start": v(2438.4, 2438.4) * mm, "end": v(3238.5, 1638.3) * mm});
            skLineSegment(sketch, "E160.0.21.1", {"start": v(3238.5, 1831.88) * mm, "end": v(2631.98, 2438.4) * mm});
            skLineSegment(sketch, "E160.0.21.2", {"start": v(2578.1, 2438.4) * mm, "end": v(3238.5, 1778) * mm});
            skLineSegment(sketch, "E160.0.22.1", {"start": v(3238.5, 1971.58) * mm, "end": v(2771.68, 2438.4) * mm});
            skLineSegment(sketch, "E160.0.22.2", {"start": v(2717.8, 2438.4) * mm, "end": v(3238.5, 1917.7) * mm});
            skLineSegment(sketch, "E160.0.23.1", {"start": v(3238.5, 2111.28) * mm, "end": v(2911.38, 2438.4) * mm});
            skLineSegment(sketch, "E160.0.23.2", {"start": v(2857.5, 2438.4) * mm, "end": v(3238.5, 2057.4) * mm});
            skLineSegment(sketch, "E160.0.24.1", {"start": v(3238.5, 2250.98) * mm, "end": v(3051.08, 2438.4) * mm});
            skLineSegment(sketch, "E160.0.24.2", {"start": v(2997.2, 2438.4) * mm, "end": v(3238.5, 2197.1) * mm});
            skLineSegment(sketch, "E160.0.25.1", {"start": v(3238.5, 2390.68) * mm, "end": v(3190.78, 2438.4) * mm});
            skLineSegment(sketch, "E160.0.25.2", {"start": v(3136.9, 2438.4) * mm, "end": v(3238.5, 2336.8) * mm});
            skLineSegment(sketch, "E160.direction1", {"start": v(2019.3, 63.5) * mm, "end": v(2044.7, 63.5) * mm, "construction": true});
            skLineSegment(sketch, "E160.direction2", {"start": v(2019.3, 63.5) * mm, "end": v(2019.3, 203.2) * mm, "construction": true});
            skLineSegment(sketch, "E161", {"start": v(2019.3, 2438.4) * mm, "end": v(2073.18, 2438.4) * mm});
            skLineSegment(sketch, "E162", {"start": v(2159, 2438.4) * mm, "end": v(2212.88, 2438.4) * mm});
            skLineSegment(sketch, "E163", {"start": v(2298.7, 2438.4) * mm, "end": v(2352.58, 2438.4) * mm});
            skLineSegment(sketch, "E164", {"start": v(2438.4, 2438.4) * mm, "end": v(2492.28, 2438.4) * mm});
            skLineSegment(sketch, "E165", {"start": v(2578.1, 2438.4) * mm, "end": v(2631.98, 2438.4) * mm});
            skLineSegment(sketch, "E166", {"start": v(2717.8, 2438.4) * mm, "end": v(2771.68, 2438.4) * mm});
            skLineSegment(sketch, "E167", {"start": v(2857.5, 2438.4) * mm, "end": v(2911.38, 2438.4) * mm});
            skLineSegment(sketch, "E168", {"start": v(2997.2, 2438.4) * mm, "end": v(3051.08, 2438.4) * mm});
            skLineSegment(sketch, "E169", {"start": v(3136.9, 2438.4) * mm, "end": v(3190.78, 2438.4) * mm});
            skLineSegment(sketch, "E170", {"start": v(3238.5, 2390.68) * mm, "end": v(3238.5, 2336.8) * mm});
            skLineSegment(sketch, "E171", {"start": v(3238.5, 2250.98) * mm, "end": v(3238.5, 2197.1) * mm});
            skLineSegment(sketch, "E172", {"start": v(3238.5, 2111.28) * mm, "end": v(3238.5, 2057.4) * mm});
            skLineSegment(sketch, "E173", {"start": v(3238.5, 1971.58) * mm, "end": v(3238.5, 1917.7) * mm});
            skLineSegment(sketch, "E174", {"start": v(3238.5, 1831.88) * mm, "end": v(3238.5, 1778) * mm});
            skLineSegment(sketch, "E175", {"start": v(3238.5, 1692.18) * mm, "end": v(3238.5, 1638.3) * mm});
            skLineSegment(sketch, "E176", {"start": v(3238.5, 1552.48) * mm, "end": v(3238.5, 1498.6) * mm});
            skLineSegment(sketch, "E177", {"start": v(3238.5, 1412.78) * mm, "end": v(3238.5, 1358.9) * mm});
            skLineSegment(sketch, "E178", {"start": v(3238.5, 1273.08) * mm, "end": v(3238.5, 1219.2) * mm});
            skLineSegment(sketch, "E179", {"start": v(3238.5, 1133.38) * mm, "end": v(3238.5, 1079.5) * mm});
            skLineSegment(sketch, "E180", {"start": v(3238.5, 993.68) * mm, "end": v(3238.5, 939.8) * mm});
            skLineSegment(sketch, "E181", {"start": v(3238.5, 853.98) * mm, "end": v(3238.5, 800.1) * mm});
            skLineSegment(sketch, "E182", {"start": v(3238.5, 714.28) * mm, "end": v(3238.5, 660.4) * mm});
            skLineSegment(sketch, "E183", {"start": v(3238.5, 574.58) * mm, "end": v(3238.5, 520.7) * mm});
            skLineSegment(sketch, "E184", {"start": v(3238.5, 434.88) * mm, "end": v(3238.5, 381) * mm});
            skLineSegment(sketch, "E185", {"start": v(3238.5, 295.18) * mm, "end": v(3238.5, 241.3) * mm});
            skLineSegment(sketch, "E186", {"start": v(3238.5, 155.48) * mm, "end": v(3238.5, 101.6) * mm});
            skLineSegment(sketch, "E187", {"start": v(3238.5, 15.78) * mm, "end": v(3238.5, 0) * mm});
            skLineSegment(sketch, "E188", {"start": v(3238.5, 0) * mm, "end": v(3200.4, 0) * mm});
            skLineSegment(sketch, "E189", {"start": v(3114.58, 0) * mm, "end": v(3060.7, 0) * mm});
            skLineSegment(sketch, "E190", {"start": v(2974.88, 0) * mm, "end": v(2921, 0) * mm});
            skLineSegment(sketch, "E191", {"start": v(2835.18, 0) * mm, "end": v(2781.3, 0) * mm});
            skLineSegment(sketch, "E192", {"start": v(2695.48, 0) * mm, "end": v(2641.6, 0) * mm});
            skLineSegment(sketch, "E193", {"start": v(2082.8, 0) * mm, "end": v(2136.68, 0) * mm});
            skLineSegment(sketch, "E194", {"start": v(2222.5, 0) * mm, "end": v(2276.38, 0) * mm});
            skLineSegment(sketch, "E195", {"start": v(2362.2, 0) * mm, "end": v(2416.08, 0) * mm});
            skLineSegment(sketch, "E196", {"start": v(2501.9, 0) * mm, "end": v(2555.78, 0) * mm});
            skLineSegment(sketch, "E197.trimOffspring", {"start": v(3444.78, 1206.5) * mm, "end": v(3365.5, 1285.78) * mm});
            skLineSegment(sketch, "E198.trimOffspring", {"start": v(3584.48, 1206.5) * mm, "end": v(3365.5, 1425.48) * mm});
            skLineSegment(sketch, "E199.trimOffspring", {"start": v(3724.18, 1206.5) * mm, "end": v(3444.78, 1485.9) * mm});
            skLineSegment(sketch, "E200.left", {"start": v(3365.5, 1425.48) * mm, "end": v(3365.5, 1371.6) * mm});
            skLineSegment(sketch, "E200.right", {"start": v(5213.35, 1393.73) * mm, "end": v(5213.35, 1339.85) * mm});
            skLineSegment(sketch, "E201.trimOffspring", {"start": v(3238.5, 1692.18) * mm, "end": v(2492.28, 2438.4) * mm});
            skLineSegment(sketch, "E202.trimOffspring", {"start": v(3390.9, 1485.9) * mm, "end": v(3670.3, 1206.5) * mm});
            skLineSegment(sketch, "E203.trimOffspring", {"start": v(3238.5, 1552.48) * mm, "end": v(2352.58, 2438.4) * mm});
            skLineSegment(sketch, "E204.trimOffspring", {"start": v(3365.5, 1371.6) * mm, "end": v(3530.6, 1206.5) * mm});
            skLineSegment(sketch, "E205.trimOffspring", {"start": v(3238.5, 1412.78) * mm, "end": v(2212.88, 2438.4) * mm});
            skLineSegment(sketch, "E206.trimOffspring", {"start": v(3365.5, 1231.9) * mm, "end": v(3390.9, 1206.5) * mm});
            skLineSegment(sketch, "E207.1.0.0", {"start": v(3876.58, 1206.5) * mm, "end": v(3597.18, 1485.9) * mm});
            skLineSegment(sketch, "E207.1.0.1", {"start": v(3543.3, 1485.9) * mm, "end": v(3822.7, 1206.5) * mm});
            skLineSegment(sketch, "E207.2.0.0", {"start": v(4028.98, 1206.5) * mm, "end": v(3749.58, 1485.9) * mm});
            skLineSegment(sketch, "E207.2.0.1", {"start": v(3695.7, 1485.9) * mm, "end": v(3975.1, 1206.5) * mm});
            skLineSegment(sketch, "E207.3.0.0", {"start": v(4181.38, 1206.5) * mm, "end": v(3901.98, 1485.9) * mm});
            skLineSegment(sketch, "E207.3.0.1", {"start": v(3848.1, 1485.9) * mm, "end": v(4127.5, 1206.5) * mm});
            skLineSegment(sketch, "E207.4.0.0", {"start": v(4333.78, 1206.5) * mm, "end": v(4054.38, 1485.9) * mm});
            skLineSegment(sketch, "E207.4.0.1", {"start": v(4000.5, 1485.9) * mm, "end": v(4279.9, 1206.5) * mm});
            skLineSegment(sketch, "E207.5.0.0", {"start": v(4486.18, 1206.5) * mm, "end": v(4206.78, 1485.9) * mm});
            skLineSegment(sketch, "E207.5.0.1", {"start": v(4152.9, 1485.9) * mm, "end": v(4432.3, 1206.5) * mm});
            skLineSegment(sketch, "E207.6.0.0", {"start": v(4638.58, 1206.5) * mm, "end": v(4359.18, 1485.9) * mm});
            skLineSegment(sketch, "E207.6.0.1", {"start": v(4305.3, 1485.9) * mm, "end": v(4584.7, 1206.5) * mm});
            skLineSegment(sketch, "E207.7.0.0", {"start": v(4790.98, 1206.5) * mm, "end": v(4511.58, 1485.9) * mm});
            skLineSegment(sketch, "E207.7.0.1", {"start": v(4457.7, 1485.9) * mm, "end": v(4737.1, 1206.5) * mm});
            skLineSegment(sketch, "E207.8.0.0", {"start": v(4943.38, 1206.5) * mm, "end": v(4663.98, 1485.9) * mm});
            skLineSegment(sketch, "E207.8.0.1", {"start": v(4610.1, 1485.9) * mm, "end": v(4889.5, 1206.5) * mm});
            skLineSegment(sketch, "E207.9.0.0", {"start": v(5095.78, 1206.5) * mm, "end": v(4816.38, 1485.9) * mm});
            skLineSegment(sketch, "E207.9.0.1", {"start": v(4762.5, 1485.9) * mm, "end": v(5041.9, 1206.5) * mm});
            skLineSegment(sketch, "E207.10.0.0", {"start": v(5213.35, 1241.33) * mm, "end": v(4968.78, 1485.9) * mm});
            skLineSegment(sketch, "E207.10.0.1", {"start": v(4914.9, 1485.9) * mm, "end": v(5194.3, 1206.5) * mm});
            skLineSegment(sketch, "E207.11.0.0", {"start": v(5213.35, 1393.73) * mm, "end": v(5121.18, 1485.9) * mm});
            skLineSegment(sketch, "E207.11.0.1", {"start": v(5067.3, 1485.9) * mm, "end": v(5213.35, 1339.85) * mm});
            skLineSegment(sketch, "E207.direction1", {"start": v(3724.18, 1206.5) * mm, "end": v(3876.58, 1206.5) * mm, "construction": true});
            skLineSegment(sketch, "E208.trimOffspring", {"start": v(5213.35, 1241.33) * mm, "end": v(5213.35, 1206.5) * mm});
            skLineSegment(sketch, "E209.trimOffspring", {"start": v(5067.3, 1485.9) * mm, "end": v(5121.18, 1485.9) * mm});
            skLineSegment(sketch, "E210.trimOffspring", {"start": v(5194.3, 1206.5) * mm, "end": v(5213.35, 1206.5) * mm});
            skLineSegment(sketch, "E211.trimOffspring", {"start": v(5041.9, 1206.5) * mm, "end": v(5095.78, 1206.5) * mm});
            skLineSegment(sketch, "E212.trimOffspring", {"start": v(4889.5, 1206.5) * mm, "end": v(4943.38, 1206.5) * mm});
            skLineSegment(sketch, "E213.trimOffspring", {"start": v(4914.9, 1485.9) * mm, "end": v(4968.78, 1485.9) * mm});
            skLineSegment(sketch, "E214.trimOffspring", {"start": v(4762.5, 1485.9) * mm, "end": v(4816.38, 1485.9) * mm});
            skLineSegment(sketch, "E215.trimOffspring", {"start": v(4610.1, 1485.9) * mm, "end": v(4663.98, 1485.9) * mm});
            skLineSegment(sketch, "E216.trimOffspring", {"start": v(4457.7, 1485.9) * mm, "end": v(4511.58, 1485.9) * mm});
            skLineSegment(sketch, "E217.trimOffspring", {"start": v(4305.3, 1485.9) * mm, "end": v(4359.18, 1485.9) * mm});
            skLineSegment(sketch, "E218.trimOffspring", {"start": v(4152.9, 1485.9) * mm, "end": v(4206.78, 1485.9) * mm});
            skLineSegment(sketch, "E219.trimOffspring", {"start": v(4432.3, 1206.5) * mm, "end": v(4638.58, 1206.5) * mm});
            skLineSegment(sketch, "E220.trimOffspring", {"start": v(4737.1, 1206.5) * mm, "end": v(4790.98, 1206.5) * mm});
            skLineSegment(sketch, "E221.trimOffspring", {"start": v(4127.5, 1206.5) * mm, "end": v(4181.38, 1206.5) * mm});
            skLineSegment(sketch, "E222.trimOffspring", {"start": v(3975.1, 1206.5) * mm, "end": v(4028.98, 1206.5) * mm});
            skLineSegment(sketch, "E223.trimOffspring", {"start": v(3530.6, 1206.5) * mm, "end": v(3876.58, 1206.5) * mm});
            skLineSegment(sketch, "E224.trimOffspring", {"start": v(3365.5, 1285.78) * mm, "end": v(3365.5, 1231.9) * mm});
            skLineSegment(sketch, "E225.trimOffspring", {"start": v(3543.3, 1485.9) * mm, "end": v(3597.18, 1485.9) * mm});
            skLineSegment(sketch, "E226.trimOffspring", {"start": v(3848.1, 1485.9) * mm, "end": v(3901.98, 1485.9) * mm});
            skLineSegment(sketch, "E227.trimOffspring", {"start": v(4000.5, 1485.9) * mm, "end": v(4054.38, 1485.9) * mm});
            skLineSegment(sketch, "E228", {"start": v(3444.78, 1485.9) * mm, "end": v(3390.9, 1485.9) * mm});
            skLineSegment(sketch, "E229", {"start": v(3444.78, 1206.5) * mm, "end": v(3390.9, 1206.5) * mm});
            skLineSegment(sketch, "E230.top", {"start": v(1892.3, 1206.5) * mm, "end": v(1854.2, 1206.5) * mm});
            skLineSegment(sketch, "E230.left", {"start": v(1892.3, 1485.9) * mm, "end": v(1892.3, 1447.8) * mm});
            skLineSegment(sketch, "E231.trimOffspring", {"start": v(2019.3, 1320.8) * mm, "end": v(3238.5, 101.6) * mm});
            skLineSegment(sketch, "E232.trimOffspring", {"start": v(1892.3, 1361.98) * mm, "end": v(1768.38, 1485.9) * mm});
            skLineSegment(sketch, "E233.trimOffspring", {"start": v(2019.3, 1181.1) * mm, "end": v(3200.4, 0) * mm});
            skLineSegment(sketch, "E234.trimOffspring", {"start": v(1892.3, 1222.28) * mm, "end": v(1628.68, 1485.9) * mm});
            skLineSegment(sketch, "E235.trimOffspring", {"start": v(2019.3, 1041.4) * mm, "end": v(3060.7, 0) * mm});
            skLineSegment(sketch, "E236.trimOffspring", {"start": v(1768.38, 1206.5) * mm, "end": v(1488.98, 1485.9) * mm});
            skLineSegment(sketch, "E237.trimOffspring", {"start": v(2019.3, 901.7) * mm, "end": v(2921, 0) * mm});
            skLineSegment(sketch, "E238.1.0.0", {"start": v(1615.98, 1206.5) * mm, "end": v(1336.58, 1485.9) * mm});
            skLineSegment(sketch, "E238.1.0.1", {"start": v(1282.7, 1485.9) * mm, "end": v(1562.1, 1206.5) * mm});
            skLineSegment(sketch, "E238.2.0.0", {"start": v(1463.58, 1206.5) * mm, "end": v(1184.18, 1485.9) * mm});
            skLineSegment(sketch, "E238.2.0.1", {"start": v(1130.3, 1485.9) * mm, "end": v(1409.7, 1206.5) * mm});
            skLineSegment(sketch, "E238.3.0.0", {"start": v(1311.18, 1206.5) * mm, "end": v(1031.78, 1485.9) * mm});
            skLineSegment(sketch, "E238.3.0.1", {"start": v(977.9, 1485.9) * mm, "end": v(1257.3, 1206.5) * mm});
            skLineSegment(sketch, "E238.4.0.0", {"start": v(1158.78, 1206.5) * mm, "end": v(879.38, 1485.9) * mm});
            skLineSegment(sketch, "E238.4.0.1", {"start": v(825.5, 1485.9) * mm, "end": v(1104.9, 1206.5) * mm});
            skLineSegment(sketch, "E238.5.0.0", {"start": v(1006.38, 1206.5) * mm, "end": v(726.98, 1485.9) * mm});
            skLineSegment(sketch, "E238.5.0.1", {"start": v(673.1, 1485.9) * mm, "end": v(952.5, 1206.5) * mm});
            skLineSegment(sketch, "E238.6.0.0", {"start": v(853.98, 1206.5) * mm, "end": v(574.58, 1485.9) * mm});
            skLineSegment(sketch, "E238.6.0.1", {"start": v(520.7, 1485.9) * mm, "end": v(800.1, 1206.5) * mm});
            skLineSegment(sketch, "E238.7.0.0", {"start": v(701.58, 1206.5) * mm, "end": v(422.18, 1485.9) * mm});
            skLineSegment(sketch, "E238.7.0.1", {"start": v(368.3, 1485.9) * mm, "end": v(647.7, 1206.5) * mm});
            skLineSegment(sketch, "E238.8.0.0", {"start": v(549.18, 1206.5) * mm, "end": v(269.78, 1485.9) * mm});
            skLineSegment(sketch, "E238.8.0.1", {"start": v(215.9, 1485.9) * mm, "end": v(495.3, 1206.5) * mm});
            skLineSegment(sketch, "E238.9.0.0", {"start": v(396.78, 1206.5) * mm, "end": v(127, 1476.28) * mm});
            skLineSegment(sketch, "E238.9.0.1", {"start": v(127, 1422.4) * mm, "end": v(342.9, 1206.5) * mm});
            skLineSegment(sketch, "E238.10.0.0", {"start": v(244.38, 1206.5) * mm, "end": v(127, 1323.88) * mm});
            skLineSegment(sketch, "E238.10.0.1", {"start": v(127, 1270) * mm, "end": v(190.5, 1206.5) * mm});
            skLineSegment(sketch, "E238.direction1", {"start": v(1768.38, 1206.5) * mm, "end": v(1714.5, 1206.5) * mm, "construction": true});
            skLineSegment(sketch, "E239.trimOffspring", {"start": v(127, 1323.88) * mm, "end": v(127, 1270) * mm});
            skLineSegment(sketch, "E240.trimOffspring", {"start": v(244.38, 1206.5) * mm, "end": v(190.5, 1206.5) * mm});
            skLineSegment(sketch, "E241.trimOffspring", {"start": v(549.18, 1206.5) * mm, "end": v(495.3, 1206.5) * mm});
            skLineSegment(sketch, "E242.trimOffspring", {"start": v(701.58, 1206.5) * mm, "end": v(647.7, 1206.5) * mm});
            skLineSegment(sketch, "E243.trimOffspring", {"start": v(853.98, 1206.5) * mm, "end": v(800.1, 1206.5) * mm});
            skLineSegment(sketch, "E244.trimOffspring", {"start": v(1006.38, 1206.5) * mm, "end": v(952.5, 1206.5) * mm});
            skLineSegment(sketch, "E245.trimOffspring", {"start": v(1158.78, 1206.5) * mm, "end": v(1104.9, 1206.5) * mm});
            skLineSegment(sketch, "E246.trimOffspring", {"start": v(269.78, 1485.9) * mm, "end": v(215.9, 1485.9) * mm});
            skLineSegment(sketch, "E247.trimOffspring", {"start": v(422.18, 1485.9) * mm, "end": v(368.3, 1485.9) * mm});
            skLineSegment(sketch, "E248.trimOffspring", {"start": v(574.58, 1485.9) * mm, "end": v(520.7, 1485.9) * mm});
            skLineSegment(sketch, "E249.trimOffspring", {"start": v(726.98, 1485.9) * mm, "end": v(673.1, 1485.9) * mm});
            skLineSegment(sketch, "E250.trimOffspring", {"start": v(1768.38, 1485.9) * mm, "end": v(1714.5, 1485.9) * mm});
            skLineSegment(sketch, "E251.trimOffspring", {"start": v(1488.98, 1485.9) * mm, "end": v(1435.1, 1485.9) * mm});
            skLineSegment(sketch, "E252.trimOffspring", {"start": v(1628.68, 1485.9) * mm, "end": v(1574.8, 1485.9) * mm});
            skLineSegment(sketch, "E253.trimOffspring", {"start": v(1336.58, 1485.9) * mm, "end": v(1282.7, 1485.9) * mm});
            skLineSegment(sketch, "E254.trimOffspring", {"start": v(1031.78, 1485.9) * mm, "end": v(977.9, 1485.9) * mm});
            skLineSegment(sketch, "E255.trimOffspring", {"start": v(879.38, 1485.9) * mm, "end": v(825.5, 1485.9) * mm});
            skLineSegment(sketch, "E256.trimOffspring", {"start": v(1311.18, 1206.5) * mm, "end": v(1257.3, 1206.5) * mm});
            skLineSegment(sketch, "E257.trimOffspring", {"start": v(1463.58, 1206.5) * mm, "end": v(1409.7, 1206.5) * mm});
            skLineSegment(sketch, "E258.trimOffspring", {"start": v(1768.38, 1206.5) * mm, "end": v(1562.1, 1206.5) * mm});
            skLineSegment(sketch, "E259.trimOffspring", {"start": v(1892.3, 1222.28) * mm, "end": v(1892.3, 1206.5) * mm});
            skLineSegment(sketch, "E260.trimOffspring", {"start": v(1892.3, 1361.98) * mm, "end": v(1892.3, 1308.1) * mm});
            skLineSegment(sketch, "E261", {"start": v(1892.3, 1485.9) * mm, "end": v(1854.2, 1485.9) * mm});
            skLineSegment(sketch, "E262", {"start": v(342.9, 1206.5) * mm, "end": v(396.78, 1206.5) * mm});
            skLineSegment(sketch, "E263", {"start": v(127, 1476.28) * mm, "end": v(127, 1422.4) * mm});
            skLineSegment(sketch, "E264", {"start": v(1130.3, 1485.9) * mm, "end": v(1184.18, 1485.9) * mm});
            skLineSegment(sketch, "E265", {"start": v(3695.7, 1485.9) * mm, "end": v(3749.58, 1485.9) * mm});
            skLineSegment(sketch, "E266", {"start": v(4279.9, 1206.5) * mm, "end": v(4333.78, 1206.5) * mm});
            skSolve(sketch);
        }
        {
            var Q0;
            Q0 = qSketchRegion(id + "F16", true);
            extrude(context, id + "F17", {"entities" : qUnion([Q0]), "oppositeDirection" : true, "depth" : 6.35 * mm});
        }
        {
            var Q0;
            Q0=makeQuery(id+"F3.opExtrude","SWEPT_FACE",FACE,{"disambiguationData":[OSD([sQuery(id+"F2.wireOp",EDGE,"E5.right")])]});
            var sketch = newSketch(context, id + "F18", { "sketchPlane" : qUnion([Q0])});
            skLineSegment(sketch, "E267.bottom", {"start": v(-1892.3, 1206.5) * mm, "end": v(-1752.6, 1206.5) * mm});
            skLineSegment(sketch, "E267.top", {"start": v(-1892.3, 12.7) * mm, "end": v(-1752.6, 12.7) * mm});
            skLineSegment(sketch, "E267.left", {"start": v(-1892.3, 1206.5) * mm, "end": v(-1892.3, 12.7) * mm});
            skLineSegment(sketch, "E267.right", {"start": v(-1752.6, 1206.5) * mm, "end": v(-1752.6, 12.7) * mm});
            skLineSegment(sketch, "E268.1.0.0", {"start": v(-1609.73, 1206.5) * mm, "end": v(-1609.73, 12.7) * mm});
            skLineSegment(sketch, "E268.1.0.1", {"start": v(-1749.43, 1206.5) * mm, "end": v(-1609.73, 1206.5) * mm});
            skLineSegment(sketch, "E268.1.0.2", {"start": v(-1749.43, 1206.5) * mm, "end": v(-1749.43, 12.7) * mm});
            skLineSegment(sketch, "E268.1.0.3", {"start": v(-1749.43, 12.7) * mm, "end": v(-1609.73, 12.7) * mm});
            skLineSegment(sketch, "E268.2.0.0", {"start": v(-1466.85, 1206.5) * mm, "end": v(-1466.85, 12.7) * mm});
            skLineSegment(sketch, "E268.2.0.1", {"start": v(-1606.55, 1206.5) * mm, "end": v(-1466.85, 1206.5) * mm});
            skLineSegment(sketch, "E268.2.0.2", {"start": v(-1606.55, 1206.5) * mm, "end": v(-1606.55, 12.7) * mm});
            skLineSegment(sketch, "E268.2.0.3", {"start": v(-1606.55, 12.7) * mm, "end": v(-1466.85, 12.7) * mm});
            skLineSegment(sketch, "E268.3.0.0", {"start": v(-1323.98, 1206.5) * mm, "end": v(-1323.98, 12.7) * mm});
            skLineSegment(sketch, "E268.3.0.1", {"start": v(-1463.67, 1206.5) * mm, "end": v(-1323.98, 1206.5) * mm});
            skLineSegment(sketch, "E268.3.0.2", {"start": v(-1463.67, 1206.5) * mm, "end": v(-1463.67, 12.7) * mm});
            skLineSegment(sketch, "E268.3.0.3", {"start": v(-1463.67, 12.7) * mm, "end": v(-1323.98, 12.7) * mm});
            skLineSegment(sketch, "E268.4.0.0", {"start": v(-1181.1, 1206.5) * mm, "end": v(-1181.1, 12.7) * mm});
            skLineSegment(sketch, "E268.4.0.1", {"start": v(-1320.8, 1206.5) * mm, "end": v(-1181.1, 1206.5) * mm});
            skLineSegment(sketch, "E268.4.0.2", {"start": v(-1320.8, 1206.5) * mm, "end": v(-1320.8, 12.7) * mm});
            skLineSegment(sketch, "E268.4.0.3", {"start": v(-1320.8, 12.7) * mm, "end": v(-1181.1, 12.7) * mm});
            skLineSegment(sketch, "E268.5.0.0", {"start": v(-1038.22, 1206.5) * mm, "end": v(-1038.22, 12.7) * mm});
            skLineSegment(sketch, "E268.5.0.1", {"start": v(-1177.92, 1206.5) * mm, "end": v(-1038.22, 1206.5) * mm});
            skLineSegment(sketch, "E268.5.0.2", {"start": v(-1177.92, 1206.5) * mm, "end": v(-1177.92, 12.7) * mm});
            skLineSegment(sketch, "E268.5.0.3", {"start": v(-1177.92, 12.7) * mm, "end": v(-1038.22, 12.7) * mm});
            skLineSegment(sketch, "E268.6.0.0", {"start": v(-895.35, 1206.5) * mm, "end": v(-895.35, 12.7) * mm});
            skLineSegment(sketch, "E268.6.0.1", {"start": v(-1035.05, 1206.5) * mm, "end": v(-895.35, 1206.5) * mm});
            skLineSegment(sketch, "E268.6.0.2", {"start": v(-1035.05, 1206.5) * mm, "end": v(-1035.05, 12.7) * mm});
            skLineSegment(sketch, "E268.6.0.3", {"start": v(-1035.05, 12.7) * mm, "end": v(-895.35, 12.7) * mm});
            skLineSegment(sketch, "E268.7.0.0", {"start": v(-752.47, 1206.5) * mm, "end": v(-752.47, 12.7) * mm});
            skLineSegment(sketch, "E268.7.0.1", {"start": v(-892.17, 1206.5) * mm, "end": v(-752.47, 1206.5) * mm});
            skLineSegment(sketch, "E268.7.0.2", {"start": v(-892.17, 1206.5) * mm, "end": v(-892.17, 12.7) * mm});
            skLineSegment(sketch, "E268.7.0.3", {"start": v(-892.17, 12.7) * mm, "end": v(-752.47, 12.7) * mm});
            skLineSegment(sketch, "E268.8.0.0", {"start": v(-609.6, 1206.5) * mm, "end": v(-609.6, 12.7) * mm});
            skLineSegment(sketch, "E268.8.0.1", {"start": v(-749.3, 1206.5) * mm, "end": v(-609.6, 1206.5) * mm});
            skLineSegment(sketch, "E268.8.0.2", {"start": v(-749.3, 1206.5) * mm, "end": v(-749.3, 12.7) * mm});
            skLineSegment(sketch, "E268.8.0.3", {"start": v(-749.3, 12.7) * mm, "end": v(-609.6, 12.7) * mm});
            skLineSegment(sketch, "E268.9.0.0", {"start": v(-466.72, 1206.5) * mm, "end": v(-466.72, 12.7) * mm});
            skLineSegment(sketch, "E268.9.0.1", {"start": v(-606.42, 1206.5) * mm, "end": v(-466.72, 1206.5) * mm});
            skLineSegment(sketch, "E268.9.0.2", {"start": v(-606.42, 1206.5) * mm, "end": v(-606.42, 12.7) * mm});
            skLineSegment(sketch, "E268.9.0.3", {"start": v(-606.42, 12.7) * mm, "end": v(-466.72, 12.7) * mm});
            skLineSegment(sketch, "E268.10.0.0", {"start": v(-323.85, 1206.5) * mm, "end": v(-323.85, 12.7) * mm});
            skLineSegment(sketch, "E268.10.0.1", {"start": v(-463.55, 1206.5) * mm, "end": v(-323.85, 1206.5) * mm});
            skLineSegment(sketch, "E268.10.0.2", {"start": v(-463.55, 1206.5) * mm, "end": v(-463.55, 12.7) * mm});
            skLineSegment(sketch, "E268.10.0.3", {"start": v(-463.55, 12.7) * mm, "end": v(-323.85, 12.7) * mm});
            skLineSegment(sketch, "E268.11.0.0", {"start": v(-180.97, 1206.5) * mm, "end": v(-180.97, 12.7) * mm});
            skLineSegment(sketch, "E268.11.0.1", {"start": v(-320.67, 1206.5) * mm, "end": v(-180.97, 1206.5) * mm});
            skLineSegment(sketch, "E268.11.0.2", {"start": v(-320.67, 1206.5) * mm, "end": v(-320.67, 12.7) * mm});
            skLineSegment(sketch, "E268.11.0.3", {"start": v(-320.67, 12.7) * mm, "end": v(-180.97, 12.7) * mm});
            skLineSegment(sketch, "E268.12.0.1", {"start": v(-177.8, 1206.5) * mm, "end": v(-130.18, 1206.5) * mm});
            skLineSegment(sketch, "E268.12.0.2", {"start": v(-177.8, 1206.5) * mm, "end": v(-177.8, 12.7) * mm});
            skLineSegment(sketch, "E268.12.0.3", {"start": v(-177.8, 12.7) * mm, "end": v(-130.18, 12.7) * mm});
            skLineSegment(sketch, "E268.direction1", {"start": v(-1752.6, 12.7) * mm, "end": v(-1609.73, 12.7) * mm, "construction": true});
            skLineSegment(sketch, "E269", {"start": v(-130.18, 1206.5) * mm, "end": v(-130.18, 12.7) * mm});
            skPoint(sketch, "E270.orphan", {"position": v(-38.1, 1206.5) * mm});
            skPoint(sketch, "E271.orphan", {"position": v(-38.1, 12.7) * mm});
            skSolve(sketch);
        }
        {
            var Q0;
            Q0 = qSketchRegion(id + "F18", true);
            extrude(context, id + "F19", {"entities" : qUnion([Q0]), "depth" : 15.88 * mm});
        }
        {
            var Q0;
            Q0=makeQuery(id+"F6.opExtrude","SWEPT_FACE",FACE,{"disambiguationData":[OSD([sQuery(id+"F5.wireOp",EDGE,"E6.right")])]});
            var sketch = newSketch(context, id + "F20", { "sketchPlane" : qUnion([Q0])});
            skLineSegment(sketch, "E272.bottom", {"start": v(-3365.5, 1206.5) * mm, "end": v(-3505.2, 1206.5) * mm});
            skLineSegment(sketch, "E272.top", {"start": v(-3365.5, 12.7) * mm, "end": v(-3505.2, 12.7) * mm});
            skLineSegment(sketch, "E272.left", {"start": v(-3365.5, 1206.5) * mm, "end": v(-3365.5, 12.7) * mm});
            skLineSegment(sketch, "E272.right", {"start": v(-3505.2, 1206.5) * mm, "end": v(-3505.2, 12.7) * mm});
            skLineSegment(sketch, "E273.1.0.0", {"start": v(-3508.38, 1206.5) * mm, "end": v(-3648.08, 1206.5) * mm});
            skLineSegment(sketch, "E273.1.0.1", {"start": v(-3508.38, 1206.5) * mm, "end": v(-3508.38, 12.7) * mm});
            skLineSegment(sketch, "E273.1.0.2", {"start": v(-3508.38, 12.7) * mm, "end": v(-3648.08, 12.7) * mm});
            skLineSegment(sketch, "E273.1.0.3", {"start": v(-3648.08, 1206.5) * mm, "end": v(-3648.08, 12.7) * mm});
            skLineSegment(sketch, "E273.2.0.0", {"start": v(-3651.25, 1206.5) * mm, "end": v(-3790.95, 1206.5) * mm});
            skLineSegment(sketch, "E273.2.0.1", {"start": v(-3651.25, 1206.5) * mm, "end": v(-3651.25, 12.7) * mm});
            skLineSegment(sketch, "E273.2.0.2", {"start": v(-3651.25, 12.7) * mm, "end": v(-3790.95, 12.7) * mm});
            skLineSegment(sketch, "E273.2.0.3", {"start": v(-3790.95, 1206.5) * mm, "end": v(-3790.95, 12.7) * mm});
            skLineSegment(sketch, "E273.3.0.0", {"start": v(-3794.13, 1206.5) * mm, "end": v(-3933.83, 1206.5) * mm});
            skLineSegment(sketch, "E273.3.0.1", {"start": v(-3794.13, 1206.5) * mm, "end": v(-3794.13, 12.7) * mm});
            skLineSegment(sketch, "E273.3.0.2", {"start": v(-3794.13, 12.7) * mm, "end": v(-3933.83, 12.7) * mm});
            skLineSegment(sketch, "E273.3.0.3", {"start": v(-3933.83, 1206.5) * mm, "end": v(-3933.83, 12.7) * mm});
            skLineSegment(sketch, "E273.4.0.0", {"start": v(-3937, 1206.5) * mm, "end": v(-4076.7, 1206.5) * mm});
            skLineSegment(sketch, "E273.4.0.1", {"start": v(-3937, 1206.5) * mm, "end": v(-3937, 12.7) * mm});
            skLineSegment(sketch, "E273.4.0.2", {"start": v(-3937, 12.7) * mm, "end": v(-4076.7, 12.7) * mm});
            skLineSegment(sketch, "E273.4.0.3", {"start": v(-4076.7, 1206.5) * mm, "end": v(-4076.7, 12.7) * mm});
            skLineSegment(sketch, "E273.5.0.0", {"start": v(-4079.88, 1206.5) * mm, "end": v(-4219.58, 1206.5) * mm});
            skLineSegment(sketch, "E273.5.0.1", {"start": v(-4079.88, 1206.5) * mm, "end": v(-4079.88, 12.7) * mm});
            skLineSegment(sketch, "E273.5.0.2", {"start": v(-4079.88, 12.7) * mm, "end": v(-4219.58, 12.7) * mm});
            skLineSegment(sketch, "E273.5.0.3", {"start": v(-4219.58, 1206.5) * mm, "end": v(-4219.58, 12.7) * mm});
            skLineSegment(sketch, "E273.6.0.0", {"start": v(-4222.75, 1206.5) * mm, "end": v(-4362.45, 1206.5) * mm});
            skLineSegment(sketch, "E273.6.0.1", {"start": v(-4222.75, 1206.5) * mm, "end": v(-4222.75, 12.7) * mm});
            skLineSegment(sketch, "E273.6.0.2", {"start": v(-4222.75, 12.7) * mm, "end": v(-4362.45, 12.7) * mm});
            skLineSegment(sketch, "E273.6.0.3", {"start": v(-4362.45, 1206.5) * mm, "end": v(-4362.45, 12.7) * mm});
            skLineSegment(sketch, "E273.7.0.0", {"start": v(-4365.63, 1206.5) * mm, "end": v(-4505.33, 1206.5) * mm});
            skLineSegment(sketch, "E273.7.0.1", {"start": v(-4365.63, 1206.5) * mm, "end": v(-4365.63, 12.7) * mm});
            skLineSegment(sketch, "E273.7.0.2", {"start": v(-4365.63, 12.7) * mm, "end": v(-4505.33, 12.7) * mm});
            skLineSegment(sketch, "E273.7.0.3", {"start": v(-4505.33, 1206.5) * mm, "end": v(-4505.33, 12.7) * mm});
            skLineSegment(sketch, "E273.8.0.0", {"start": v(-4508.5, 1206.5) * mm, "end": v(-4648.2, 1206.5) * mm});
            skLineSegment(sketch, "E273.8.0.1", {"start": v(-4508.5, 1206.5) * mm, "end": v(-4508.5, 12.7) * mm});
            skLineSegment(sketch, "E273.8.0.2", {"start": v(-4508.5, 12.7) * mm, "end": v(-4648.2, 12.7) * mm});
            skLineSegment(sketch, "E273.8.0.3", {"start": v(-4648.2, 1206.5) * mm, "end": v(-4648.2, 12.7) * mm});
            skLineSegment(sketch, "E273.9.0.0", {"start": v(-4651.38, 1206.5) * mm, "end": v(-4791.08, 1206.5) * mm});
            skLineSegment(sketch, "E273.9.0.1", {"start": v(-4651.38, 1206.5) * mm, "end": v(-4651.38, 12.7) * mm});
            skLineSegment(sketch, "E273.9.0.2", {"start": v(-4651.38, 12.7) * mm, "end": v(-4791.08, 12.7) * mm});
            skLineSegment(sketch, "E273.9.0.3", {"start": v(-4791.08, 1206.5) * mm, "end": v(-4791.08, 12.7) * mm});
            skLineSegment(sketch, "E273.10.0.0", {"start": v(-4794.25, 1206.5) * mm, "end": v(-4933.95, 1206.5) * mm});
            skLineSegment(sketch, "E273.10.0.1", {"start": v(-4794.25, 1206.5) * mm, "end": v(-4794.25, 12.7) * mm});
            skLineSegment(sketch, "E273.10.0.2", {"start": v(-4794.25, 12.7) * mm, "end": v(-4933.95, 12.7) * mm});
            skLineSegment(sketch, "E273.10.0.3", {"start": v(-4933.95, 1206.5) * mm, "end": v(-4933.95, 12.7) * mm});
            skLineSegment(sketch, "E273.11.0.0", {"start": v(-4937.13, 1206.5) * mm, "end": v(-5076.83, 1206.5) * mm});
            skLineSegment(sketch, "E273.11.0.1", {"start": v(-4937.13, 1206.5) * mm, "end": v(-4937.13, 12.7) * mm});
            skLineSegment(sketch, "E273.11.0.2", {"start": v(-4937.13, 12.7) * mm, "end": v(-5076.83, 12.7) * mm});
            skLineSegment(sketch, "E273.11.0.3", {"start": v(-5076.83, 1206.5) * mm, "end": v(-5076.83, 12.7) * mm});
            skLineSegment(sketch, "E273.12.0.0", {"start": v(-5080, 1206.5) * mm, "end": v(-5210.18, 1206.5) * mm});
            skLineSegment(sketch, "E273.12.0.1", {"start": v(-5080, 1206.5) * mm, "end": v(-5080, 12.7) * mm});
            skLineSegment(sketch, "E273.12.0.2", {"start": v(-5080, 12.7) * mm, "end": v(-5210.18, 12.7) * mm});
            skLineSegment(sketch, "E273.direction1", {"start": v(-3505.2, 1206.5) * mm, "end": v(-3648.08, 1206.5) * mm, "construction": true});
            skLineSegment(sketch, "E274", {"start": v(-5210.18, 1206.5) * mm, "end": v(-5210.18, 12.7) * mm});
            skPoint(sketch, "E274.endSnap0", {"position": v(-5149.85, 12.7) * mm});
            skPoint(sketch, "E273.12.0.3.end.orphan", {"position": v(-5219.7, 12.7) * mm});
            skPoint(sketch, "E275.orphan", {"position": v(-5219.7, 1206.5) * mm});
            skSolve(sketch);
        }
        {
            var Q0;
            Q0 = qSketchRegion(id + "F20", true);
            extrude(context, id + "F21", {"entities" : qUnion([Q0]), "depth" : 15.88 * mm});
        }
        {
            var Q0;
            Q0=makeQuery(id+"F21.opExtrude","CAP_FACE",FACE,{"disambiguationData":[OSD([sQuery(id+"F20.wireOp",EDGE,"E272.bottom"),sQuery(id+"F20.wireOp",EDGE,"E272.top"),sQuery(id+"F20.wireOp",EDGE,"E272.left"),sQuery(id+"F20.wireOp",EDGE,"E272.right")])],"isStart":false});
            var sketch = newSketch(context, id + "F22", { "sketchPlane" : qUnion([Q0])});
            skLineSegment(sketch, "E276.bottom", {"start": v(-3365.5, 1206.5) * mm, "end": v(-5213.35, 1206.5) * mm});
            skLineSegment(sketch, "E276.top", {"start": v(-3365.5, 1117.6) * mm, "end": v(-5213.35, 1117.6) * mm});
            skLineSegment(sketch, "E276.left", {"start": v(-3365.5, 1206.5) * mm, "end": v(-3365.5, 1117.6) * mm});
            skLineSegment(sketch, "E276.right", {"start": v(-5213.35, 1206.5) * mm, "end": v(-5213.35, 1117.6) * mm});
            skLineSegment(sketch, "E277.bottom", {"start": v(-3365.5, 12.7) * mm, "end": v(-5213.35, 12.7) * mm});
            skLineSegment(sketch, "E277.top", {"start": v(-3365.5, 101.6) * mm, "end": v(-5213.35, 101.6) * mm});
            skLineSegment(sketch, "E277.left", {"start": v(-3365.5, 12.7) * mm, "end": v(-3365.5, 101.6) * mm});
            skLineSegment(sketch, "E277.right", {"start": v(-5213.35, 12.7) * mm, "end": v(-5213.35, 101.6) * mm});
            skSolve(sketch);
        }
        {
            var Q0;
            Q0 = qSketchRegion(id + "F22", true);
            extrude(context, id + "F23", {"entities" : qUnion([Q0]), "depth" : 15.88 * mm});
        }
        {
            var Q0;
            Q0=makeQuery(id+"F19.opExtrude","CAP_FACE",FACE,{"disambiguationData":[OSD([sQuery(id+"F18.wireOp",EDGE,"E267.bottom"),sQuery(id+"F18.wireOp",EDGE,"E267.top"),sQuery(id+"F18.wireOp",EDGE,"E267.left"),sQuery(id+"F18.wireOp",EDGE,"E267.right")])],"isStart":false});
            var sketch = newSketch(context, id + "F24", { "sketchPlane" : qUnion([Q0])});
            skLineSegment(sketch, "E278.bottom", {"start": v(-1892.3, 1206.5) * mm, "end": v(-127, 1206.5) * mm});
            skLineSegment(sketch, "E278.top", {"start": v(-1892.3, 1117.6) * mm, "end": v(-127, 1117.6) * mm});
            skLineSegment(sketch, "E278.left", {"start": v(-1892.3, 1206.5) * mm, "end": v(-1892.3, 1117.6) * mm});
            skLineSegment(sketch, "E278.right", {"start": v(-127, 1206.5) * mm, "end": v(-127, 1117.6) * mm});
            skLineSegment(sketch, "E279.bottom", {"start": v(-1892.3, 12.7) * mm, "end": v(-127, 12.7) * mm});
            skLineSegment(sketch, "E279.top", {"start": v(-1892.3, 101.6) * mm, "end": v(-127, 101.6) * mm});
            skLineSegment(sketch, "E279.left", {"start": v(-1892.3, 12.7) * mm, "end": v(-1892.3, 101.6) * mm});
            skLineSegment(sketch, "E279.right", {"start": v(-127, 12.7) * mm, "end": v(-127, 101.6) * mm});
            skSolve(sketch);
        }
        {
            var Q0;
            Q0 = qSketchRegion(id + "F24", true);
            extrude(context, id + "F25", {"entities" : qUnion([Q0]), "depth" : 15.88 * mm});
        }
        {
            var Q0;
            Q0=makeQuery(id+"F1.opExtrude","SWEPT_FACE",FACE,{"disambiguationData":[OSD([sQuery(id+"F0.wireOp",EDGE,"E4.right")])]});
            var sketch = newSketch(context, id + "F26", { "sketchPlane" : qUnion([Q0])});
            skLineSegment(sketch, "E280.bottom", {"start": v(-107.95, 1485.9) * mm, "end": v(19.05, 1485.9) * mm});
            skLineSegment(sketch, "E280.top", {"start": v(-107.95, 1524) * mm, "end": v(19.05, 1524) * mm});
            skLineSegment(sketch, "E280.left", {"start": v(-107.95, 1485.9) * mm, "end": v(-107.95, 1524) * mm});
            skLineSegment(sketch, "E280.right", {"start": v(19.05, 1485.9) * mm, "end": v(19.05, 1524) * mm});
            skSolve(sketch);
        }
        {
            var Q0;
            Q0 = qSketchRegion(id + "F26", true);
            var Q1;
            Q1=makeQuery(id+"F10.opExtrude","SWEPT_FACE",FACE,{"disambiguationData":[OSD([sQuery(id+"F9.wireOp",EDGE,"E9.left")])]});
            extrude(context, id + "F27", {"entities" : qUnion([Q0]), "endBound" : BoundingType.UP_TO_SURFACE, "oppositeDirection" : true, "endBoundEntityFace" : qUnion([Q1]), "depth" : 25.4 * mm});
        }
        {
            var Q0;
            Q0=makeQuery(id+"F1.opExtrude","SWEPT_FACE",FACE,{"disambiguationData":[OSD([sQuery(id+"F0.wireOp",EDGE,"E1.left")])]});
            var sketch = newSketch(context, id + "F28", { "sketchPlane" : qUnion([Q0])});
            skLineSegment(sketch, "E281.bottom", {"start": v(-19.05, 1485.9) * mm, "end": v(107.95, 1485.9) * mm});
            skLineSegment(sketch, "E281.top", {"start": v(-19.05, 1524) * mm, "end": v(107.95, 1524) * mm});
            skLineSegment(sketch, "E281.left", {"start": v(-19.05, 1485.9) * mm, "end": v(-19.05, 1524) * mm});
            skLineSegment(sketch, "E281.right", {"start": v(107.95, 1485.9) * mm, "end": v(107.95, 1524) * mm});
            skSolve(sketch);
        }
        {
            var Q0;
            Q0 = qSketchRegion(id + "F28", true);
            var Q1;
            Q1=makeQuery(id+"F8.opExtrude","SWEPT_FACE",FACE,{"disambiguationData":[OSD([sQuery(id+"F7.wireOp",EDGE,"E8.left")])]});
            extrude(context, id + "F29", {"entities" : qUnion([Q0]), "endBound" : BoundingType.UP_TO_SURFACE, "oppositeDirection" : true, "endBoundEntityFace" : qUnion([Q1]), "depth" : 25.4 * mm});
        }
        {
            var Q0;
            Q0=makeQuery(id+"F27.opExtrude","SWEPT_EDGE",EDGE,{"disambiguationData":[OSD([sQuery(id+"F26.wireOp",EDGE,"E280.top"),sQuery(id+"F26.wireOp",EDGE,"E280.right")])]});
            var Q1;
            Q1=makeQuery(id+"F27.opExtrude","SWEPT_EDGE",EDGE,{"disambiguationData":[OSD([sQuery(id+"F26.wireOp",EDGE,"E280.top"),sQuery(id+"F26.wireOp",EDGE,"E280.left")])]});
            var Q2;
            Q2=makeQuery(id+"F29.opExtrude","SWEPT_EDGE",EDGE,{"disambiguationData":[OSD([sQuery(id+"F28.wireOp",EDGE,"E281.top"),sQuery(id+"F28.wireOp",EDGE,"E281.left")])]});
            var Q3;
            Q3=makeQuery(id+"F29.opExtrude","SWEPT_EDGE",EDGE,{"disambiguationData":[OSD([sQuery(id+"F28.wireOp",EDGE,"E281.top"),sQuery(id+"F28.wireOp",EDGE,"E281.right")])]});
            chamfer(context, id + "F30", {"entities" : qUnion([Q0, Q1, Q2, Q3]), "width" : 5.08 * mm, "tangentPropagation" : true});
        }
    });
